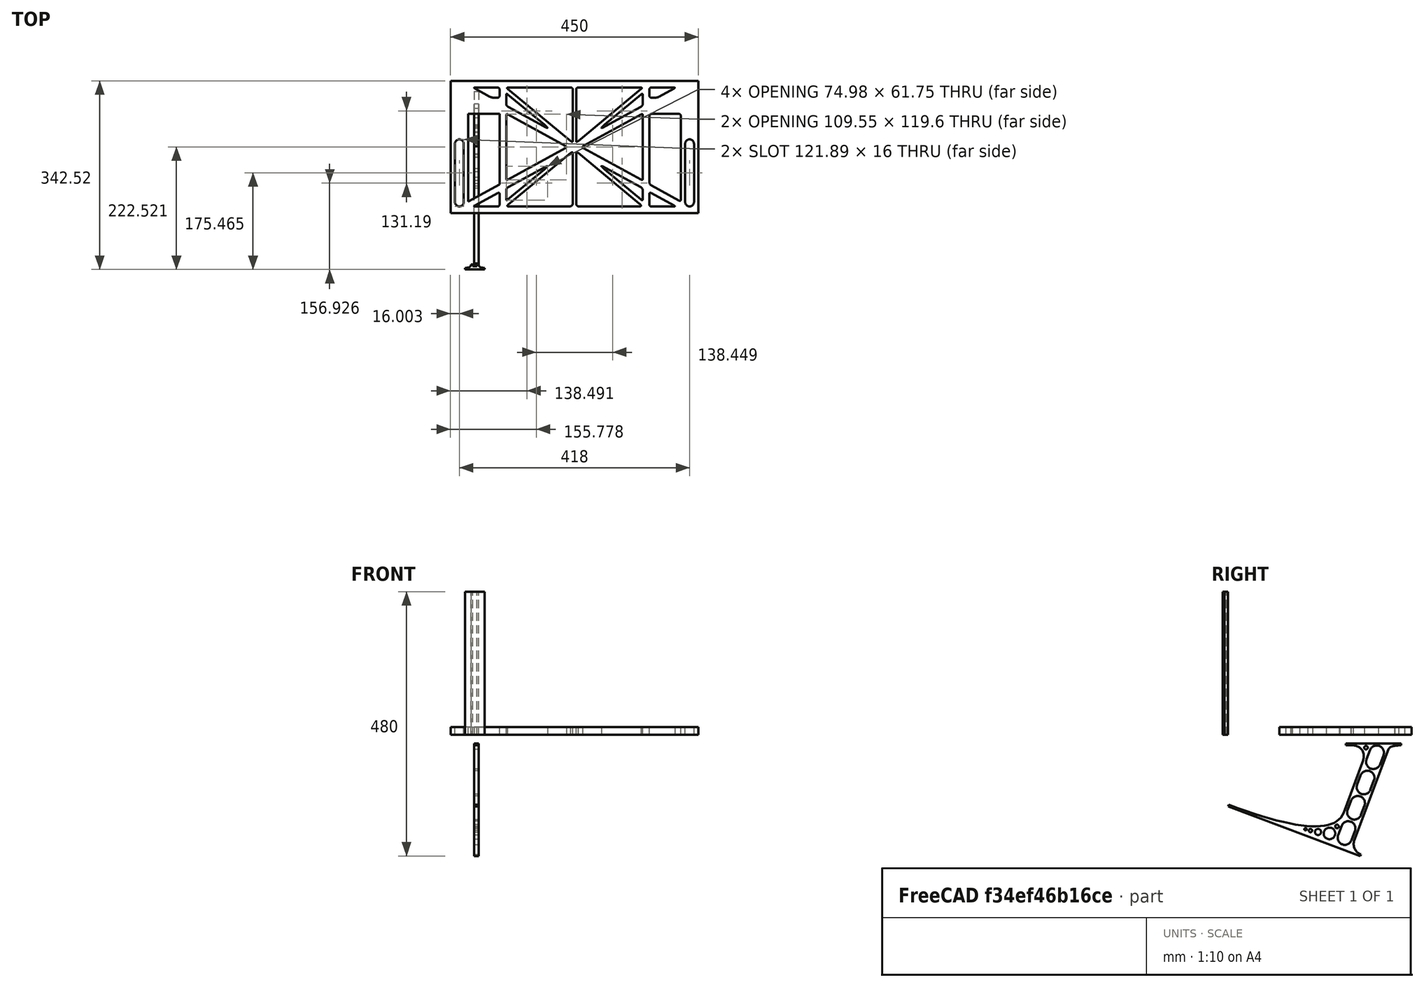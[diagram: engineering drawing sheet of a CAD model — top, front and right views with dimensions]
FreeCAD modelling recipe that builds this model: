
FCSTD DOCUMENT  (FreeCAD 0.19R0.19.2)
Label: laptopStand144FCStd
License: All rights reserved
LicenseURL: http://en.wikipedia.org/wiki/All_rights_reserved
objects: Sketcher::SketchObject×4, Part::Extrusion×3
note: 7 computed .brp shape members not serialized (recipe doc carries the construction recipe); baked Part::Feature solids carry a one-line shape summary decoded from their .brp

FEATURE [Sketcher::SketchObject] Sketch
  FullyConstrained = false
  sketch-geometry (349):
    g0: LineSegment StartX=-10.9272 StartY=-82.7794 StartZ=0 EndX=46.0728 EndY=-51.4823 EndZ=0
    g1: LineSegment StartX=-10.9272 StartY=76.4095 StartZ=0 EndX=-10.9272 EndY=-82.7794 EndZ=0
    g2: LineSegment StartX=46.0728 StartY=76.4095 StartZ=0 EndX=46.0728 EndY=-51.4823 EndZ=0
    g3: LineSegment StartX=-42.9272 StartY=136.221 StartZ=0 EndX=-42.9272 EndY=-103.779 EndZ=0
    g4: LineSegment StartX=407.073 StartY=136.221 StartZ=0 EndX=407.073 EndY=-103.779 EndZ=0
    g5: ArcOfCircle CenterX=-26.9272 CenterY=-83.7794 CenterZ=0 NormalX=0 NormalY=0 NormalZ=1 AngleXU=0 Radius=8 StartAngle=3.14159 EndAngle=6.28319
    g6: ArcOfCircle CenterX=391.073 CenterY=22.1087 CenterZ=0 NormalX=0 NormalY=0 NormalZ=1 AngleXU=0 Radius=8 StartAngle=-4.4e-15 EndAngle=3.14159
    g7: LineSegment StartX=399.073 StartY=22.1087 StartZ=0 EndX=399.073 EndY=-83.7794 EndZ=0
    g8: LineSegment StartX=383.073 StartY=22.1087 StartZ=0 EndX=383.073 EndY=-83.7794 EndZ=0
    g9: ArcOfCircle CenterX=391.073 CenterY=-83.7794 CenterZ=0 NormalX=0 NormalY=0 NormalZ=1 AngleXU=0 Radius=8 StartAngle=3.14159 EndAngle=6.28319
    g10: Circle CenterX=175.022 CenterY=27.0628 CenterZ=0 NormalX=0 NormalY=0 NormalZ=1 AngleXU=0 Radius=1
    g11: Circle CenterX=179.022 CenterY=24.8665 CenterZ=0 NormalX=0 NormalY=0 NormalZ=1 AngleXU=0 Radius=1
    g12: Circle CenterX=179.022 CenterY=27.0628 CenterZ=0 NormalX=0 NormalY=0 NormalZ=1 AngleXU=0 Radius=1
    g13: BSplineCurve PolesCount=3 KnotsCount=2 Degree=2 IsPeriodic=0
    g14: GeomPoint X=175.022 Y=27.0628 Z=0
    g15: GeomPoint X=179.022 Y=27.0628 Z=0
    g16: Circle CenterX=189.124 CenterY=27.0628 CenterZ=0 NormalX=0 NormalY=0 NormalZ=1 AngleXU=0 Radius=1
    g17: Circle CenterX=185.124 CenterY=24.8665 CenterZ=0 NormalX=0 NormalY=0 NormalZ=1 AngleXU=0 Radius=1
    g18: Circle CenterX=185.124 CenterY=27.0628 CenterZ=0 NormalX=0 NormalY=0 NormalZ=1 AngleXU=0 Radius=1
    g19: BSplineCurve PolesCount=3 KnotsCount=2 Degree=2 IsPeriodic=0
    g20: GeomPoint X=189.124 Y=27.0628 Z=0
    g21: GeomPoint X=185.124 Y=27.0628 Z=0
    g22: Circle CenterX=175.022 CenterY=5.37834 CenterZ=0 NormalX=0 NormalY=0 NormalZ=1 AngleXU=0 Radius=1
    g23: Circle CenterX=179.022 CenterY=7.57463 CenterZ=0 NormalX=0 NormalY=0 NormalZ=1 AngleXU=0 Radius=1
    g24: Circle CenterX=179.022 CenterY=5.34704 CenterZ=0 NormalX=0 NormalY=0 NormalZ=1 AngleXU=0 Radius=1
    g25: BSplineCurve PolesCount=3 KnotsCount=2 Degree=2 IsPeriodic=0
    g26: GeomPoint X=175.022 Y=5.37834 Z=0
    g27: GeomPoint X=179.022 Y=5.34704 Z=0
    g28: Circle CenterX=189.124 CenterY=5.37834 CenterZ=0 NormalX=0 NormalY=0 NormalZ=1 AngleXU=0 Radius=1
    g29: Circle CenterX=185.124 CenterY=7.57463 CenterZ=0 NormalX=0 NormalY=0 NormalZ=1 AngleXU=0 Radius=1
    g30: Circle CenterX=185.124 CenterY=5.34704 CenterZ=0 NormalX=0 NormalY=0 NormalZ=1 AngleXU=0 Radius=1
    g31: BSplineCurve PolesCount=3 KnotsCount=2 Degree=2 IsPeriodic=0
    g32: GeomPoint X=189.124 Y=5.37834 Z=0
    g33: GeomPoint X=185.124 Y=5.34704 Z=0
    g34: Circle CenterX=165.871 CenterY=18.1458 CenterZ=0 NormalX=0 NormalY=0 NormalZ=1 AngleXU=0 Radius=1
    g35: Circle CenterX=169.377 CenterY=16.2206 CenterZ=0 NormalX=0 NormalY=0 NormalZ=1 AngleXU=0 Radius=1
    g36: Circle CenterX=165.871 CenterY=14.2954 CenterZ=0 NormalX=0 NormalY=0 NormalZ=1 AngleXU=0 Radius=1
    g37: BSplineCurve PolesCount=3 KnotsCount=2 Degree=2 IsPeriodic=0
    g38: GeomPoint X=165.871 Y=18.1458 Z=0
    g39: GeomPoint X=165.871 Y=14.2954 Z=0
    g40: Circle CenterX=198.275 CenterY=18.1458 CenterZ=0 NormalX=0 NormalY=0 NormalZ=1 AngleXU=0 Radius=1
    g41: Circle CenterX=194.768 CenterY=16.2206 CenterZ=0 NormalX=0 NormalY=0 NormalZ=1 AngleXU=0 Radius=1
    g42: Circle CenterX=198.275 CenterY=14.2954 CenterZ=0 NormalX=0 NormalY=0 NormalZ=1 AngleXU=0 Radius=1
    g43: BSplineCurve PolesCount=3 KnotsCount=2 Degree=2 IsPeriodic=0
    g44: GeomPoint X=198.275 Y=18.1458 Z=0
    g45: GeomPoint X=198.275 Y=14.2954 Z=0
    g46: LineSegment StartX=407.073 StartY=-103.779 StartZ=0 EndX=-42.9272 EndY=-103.779 EndZ=0
    g47: LineSegment StartX=407.073 StartY=136.221 StartZ=0 EndX=-42.9272 EndY=136.221 EndZ=0
    g48: LineSegment StartX=46.0728 StartY=76.4095 StartZ=0 EndX=-10.9272 EndY=76.4095 EndZ=0
    g49: Circle CenterX=125.607 CenterY=54.1951 CenterZ=0 NormalX=0 NormalY=0 NormalZ=1 AngleXU=0 Radius=1
    g50: Circle CenterX=139.632 CenterY=46.4944 CenterZ=0 NormalX=0 NormalY=0 NormalZ=1 AngleXU=0 Radius=1
    g51: Circle CenterX=127.326 CenterY=56.7187 CenterZ=0 NormalX=0 NormalY=0 NormalZ=1 AngleXU=0 Radius=1
    g52: BSplineCurve PolesCount=3 KnotsCount=2 Degree=2 IsPeriodic=0
    g53: GeomPoint X=125.607 Y=54.1951 Z=0
    g54: GeomPoint X=127.326 Y=56.7187 Z=0
    g55: Circle CenterX=236.821 CenterY=56.7187 CenterZ=0 NormalX=0 NormalY=0 NormalZ=1 AngleXU=0 Radius=1
    g56: Circle CenterX=224.513 CenterY=46.4944 CenterZ=0 NormalX=0 NormalY=0 NormalZ=1 AngleXU=0 Radius=1
    g57: Circle CenterX=238.538 CenterY=54.1951 CenterZ=0 NormalX=0 NormalY=0 NormalZ=1 AngleXU=0 Radius=1
    g58: BSplineCurve PolesCount=3 KnotsCount=2 Degree=2 IsPeriodic=0
    g59: GeomPoint X=236.821 Y=56.7187 Z=0
    g60: GeomPoint X=238.538 Y=54.1951 Z=0
    g61: Circle CenterX=238.538 CenterY=-21.7539 CenterZ=0 NormalX=0 NormalY=0 NormalZ=1 AngleXU=0 Radius=1
    g62: Circle CenterX=224.513 CenterY=-14.0532 CenterZ=0 NormalX=0 NormalY=0 NormalZ=1 AngleXU=0 Radius=1
    g63: Circle CenterX=236.821 CenterY=-24.2775 CenterZ=0 NormalX=0 NormalY=0 NormalZ=1 AngleXU=0 Radius=1
    g64: BSplineCurve PolesCount=3 KnotsCount=2 Degree=2 IsPeriodic=0
    g65: GeomPoint X=238.538 Y=-21.7539 Z=0
    g66: GeomPoint X=236.821 Y=-24.2775 Z=0
    g67: Circle CenterX=125.607 CenterY=-21.7539 CenterZ=0 NormalX=0 NormalY=0 NormalZ=1 AngleXU=0 Radius=1
    g68: Circle CenterX=139.632 CenterY=-14.0532 CenterZ=0 NormalX=0 NormalY=0 NormalZ=1 AngleXU=0 Radius=1
    g69: Circle CenterX=127.325 CenterY=-24.2775 CenterZ=0 NormalX=0 NormalY=0 NormalZ=1 AngleXU=0 Radius=1
    g70: BSplineCurve PolesCount=3 KnotsCount=2 Degree=2 IsPeriodic=0
    g71: GeomPoint X=125.607 Y=-21.7539 Z=0
    g72: GeomPoint X=127.325 Y=-24.2775 Z=0
    g73: Circle CenterX=302.996 CenterY=111.695 CenterZ=0 NormalX=0 NormalY=0 NormalZ=1 AngleXU=0 Radius=1
    g74: Circle CenterX=306.073 CenterY=114.251 CenterZ=0 NormalX=0 NormalY=0 NormalZ=1 AngleXU=0 Radius=1
    g75: Circle CenterX=306.073 CenterY=110.251 CenterZ=0 NormalX=0 NormalY=0 NormalZ=1 AngleXU=0 Radius=1
    g76: BSplineCurve PolesCount=3 KnotsCount=2 Degree=2 IsPeriodic=0
    g77: GeomPoint X=302.996 Y=111.695 Z=0
    g78: GeomPoint X=306.073 Y=110.251 Z=0
    g79: Circle CenterX=306.073 CenterY=95.2763 CenterZ=0 NormalX=0 NormalY=0 NormalZ=1 AngleXU=0 Radius=1
    g80: Circle CenterX=306.073 CenterY=91.2763 CenterZ=0 NormalX=0 NormalY=0 NormalZ=1 AngleXU=0 Radius=1
    g81: Circle CenterX=302.567 CenterY=89.3511 CenterZ=0 NormalX=0 NormalY=0 NormalZ=1 AngleXU=0 Radius=1
    g82: BSplineCurve PolesCount=3 KnotsCount=2 Degree=2 IsPeriodic=0
    g83: GeomPoint X=306.073 Y=95.2763 Z=0
    g84: GeomPoint X=302.567 Y=89.3511 Z=0
    g85: LineSegment StartX=306.073 StartY=110.251 StartZ=0 EndX=306.073 EndY=95.2763 EndZ=0
    g86: LineSegment StartX=302.996 StartY=111.695 StartZ=0 EndX=236.821 EndY=56.7187 EndZ=0
    g87: LineSegment StartX=238.538 StartY=54.1951 StartZ=0 EndX=302.567 EndY=89.3511 EndZ=0
    g88: Circle CenterX=61.1496 CenterY=111.695 CenterZ=0 NormalX=0 NormalY=0 NormalZ=1 AngleXU=0 Radius=1
    g89: Circle CenterX=58.0728 CenterY=114.251 CenterZ=0 NormalX=0 NormalY=0 NormalZ=1 AngleXU=0 Radius=1
    g90: Circle CenterX=58.0728 CenterY=110.251 CenterZ=0 NormalX=0 NormalY=0 NormalZ=1 AngleXU=0 Radius=1
    g91: BSplineCurve PolesCount=3 KnotsCount=2 Degree=2 IsPeriodic=0
    g92: GeomPoint X=61.1496 Y=111.695 Z=0
    g93: GeomPoint X=58.0728 Y=110.251 Z=0
    g94: Circle CenterX=61.5791 CenterY=89.3511 CenterZ=0 NormalX=0 NormalY=0 NormalZ=1 AngleXU=0 Radius=1
    g95: Circle CenterX=58.0728 CenterY=91.2763 CenterZ=0 NormalX=0 NormalY=0 NormalZ=1 AngleXU=0 Radius=1
    g96: Circle CenterX=58.0728 CenterY=95.2763 CenterZ=0 NormalX=0 NormalY=0 NormalZ=1 AngleXU=0 Radius=1
    g97: BSplineCurve PolesCount=3 KnotsCount=2 Degree=2 IsPeriodic=0
    g98: GeomPoint X=61.5791 Y=89.3511 Z=0
    g99: GeomPoint X=58.0728 Y=95.2763 Z=0
    g100: LineSegment StartX=58.0728 StartY=110.251 StartZ=0 EndX=58.0728 EndY=95.2763 EndZ=0
    g101: LineSegment StartX=61.1496 StartY=111.695 StartZ=0 EndX=127.326 EndY=56.7187 EndZ=0
    g102: LineSegment StartX=125.607 StartY=54.1951 StartZ=0 EndX=61.5791 EndY=89.3511 EndZ=0
    g103: Circle CenterX=61.5791 CenterY=-56.9099 CenterZ=0 NormalX=0 NormalY=0 NormalZ=1 AngleXU=0 Radius=1
    g104: Circle CenterX=58.0728 CenterY=-58.8351 CenterZ=0 NormalX=0 NormalY=0 NormalZ=1 AngleXU=0 Radius=1
    g105: Circle CenterX=58.0728 CenterY=-62.8351 CenterZ=0 NormalX=0 NormalY=0 NormalZ=1 AngleXU=0 Radius=1
    g106: BSplineCurve PolesCount=3 KnotsCount=2 Degree=2 IsPeriodic=0
    g107: GeomPoint X=61.5791 Y=-56.9099 Z=0
    g108: GeomPoint X=58.0728 Y=-62.8351 Z=0
    g109: Circle CenterX=58.0728 CenterY=-77.8102 CenterZ=0 NormalX=0 NormalY=0 NormalZ=1 AngleXU=0 Radius=1
    g110: Circle CenterX=58.0728 CenterY=-81.8102 CenterZ=0 NormalX=0 NormalY=0 NormalZ=1 AngleXU=0 Radius=1
    g111: Circle CenterX=61.1496 CenterY=-79.2541 CenterZ=0 NormalX=0 NormalY=0 NormalZ=1 AngleXU=0 Radius=1
    g112: BSplineCurve PolesCount=3 KnotsCount=2 Degree=2 IsPeriodic=0
    g113: GeomPoint X=58.0728 Y=-77.8102 Z=0
    g114: GeomPoint X=61.1496 Y=-79.2541 Z=0
    g115: LineSegment StartX=58.0728 StartY=-62.8351 StartZ=0 EndX=58.0728 EndY=-77.8102 EndZ=0
    g116: LineSegment StartX=61.1496 StartY=-79.2541 StartZ=0 EndX=127.325 EndY=-24.2775 EndZ=0
    g117: LineSegment StartX=125.607 StartY=-21.7539 StartZ=0 EndX=61.5791 EndY=-56.9099 EndZ=0
    g118: Circle CenterX=302.567 CenterY=-56.9099 CenterZ=0 NormalX=0 NormalY=0 NormalZ=1 AngleXU=0 Radius=1
    g119: Circle CenterX=306.073 CenterY=-58.8351 CenterZ=0 NormalX=0 NormalY=0 NormalZ=1 AngleXU=0 Radius=1
    g120: Circle CenterX=306.073 CenterY=-62.8351 CenterZ=0 NormalX=0 NormalY=0 NormalZ=1 AngleXU=0 Radius=1
    g121: BSplineCurve PolesCount=3 KnotsCount=2 Degree=2 IsPeriodic=0
    g122: GeomPoint X=302.567 Y=-56.9099 Z=0
    g123: GeomPoint X=306.073 Y=-62.8351 Z=0
    g124: Circle CenterX=302.996 CenterY=-79.2541 CenterZ=0 NormalX=0 NormalY=0 NormalZ=1 AngleXU=0 Radius=1
    g125: Circle CenterX=306.073 CenterY=-81.8102 CenterZ=0 NormalX=0 NormalY=0 NormalZ=1 AngleXU=0 Radius=1
    g126: Circle CenterX=306.073 CenterY=-77.8102 CenterZ=0 NormalX=0 NormalY=0 NormalZ=1 AngleXU=0 Radius=1
    g127: BSplineCurve PolesCount=3 KnotsCount=2 Degree=2 IsPeriodic=0
    g128: GeomPoint X=302.996 Y=-79.2541 Z=0
    g129: GeomPoint X=306.073 Y=-77.8102 Z=0
    g130: LineSegment StartX=306.073 StartY=-62.8351 StartZ=0 EndX=306.073 EndY=-77.8102 EndZ=0
    g131: LineSegment StartX=302.996 StartY=-79.2541 StartZ=0 EndX=236.821 EndY=-24.2775 EndZ=0
    g132: LineSegment StartX=238.538 StartY=-21.7539 StartZ=0 EndX=302.567 EndY=-56.9099 EndZ=0
    g133: Circle CenterX=61.6457 CenterY=-88.8112 CenterZ=0 NormalX=0 NormalY=0 NormalZ=1 AngleXU=0 Radius=1
    g134: Circle CenterX=58.0728 CenterY=-91.7794 CenterZ=0 NormalX=0 NormalY=0 NormalZ=1 AngleXU=0 Radius=1
    g135: Circle CenterX=63.9135 CenterY=-91.7794 CenterZ=0 NormalX=0 NormalY=0 NormalZ=1 AngleXU=0 Radius=1
    g136: BSplineCurve PolesCount=3 KnotsCount=2 Degree=2 IsPeriodic=0
    g137: GeomPoint X=61.6457 Y=-88.8112 Z=0
    g138: GeomPoint X=63.9135 Y=-91.7794 Z=0
    g139: Circle CenterX=179.022 CenterY=-85.8163 CenterZ=0 NormalX=0 NormalY=0 NormalZ=1 AngleXU=0 Radius=1
    g140: Circle CenterX=179.022 CenterY=-91.7794 CenterZ=0 NormalX=0 NormalY=0 NormalZ=1 AngleXU=0 Radius=1
    g141: Circle CenterX=171.895 CenterY=-91.7794 CenterZ=0 NormalX=0 NormalY=0 NormalZ=1 AngleXU=0 Radius=1
    g142: BSplineCurve PolesCount=3 KnotsCount=2 Degree=2 IsPeriodic=0
    g143: GeomPoint X=179.022 Y=-85.8163 Z=0
    g144: GeomPoint X=171.895 Y=-91.7794 Z=0
    g145: Circle CenterX=185.124 CenterY=-86.2028 CenterZ=0 NormalX=0 NormalY=0 NormalZ=1 AngleXU=0 Radius=1
    g146: Circle CenterX=185.124 CenterY=-91.7794 CenterZ=0 NormalX=0 NormalY=0 NormalZ=1 AngleXU=0 Radius=1
    g147: Circle CenterX=191.747 CenterY=-91.7794 CenterZ=0 NormalX=0 NormalY=0 NormalZ=1 AngleXU=0 Radius=1
    g148: BSplineCurve PolesCount=3 KnotsCount=2 Degree=2 IsPeriodic=0
    g149: GeomPoint X=185.124 Y=-86.2028 Z=0
    g150: GeomPoint X=191.747 Y=-91.7794 Z=0
    g151: Circle CenterX=299.888 CenterY=-86.6413 CenterZ=0 NormalX=0 NormalY=0 NormalZ=1 AngleXU=0 Radius=1
    g152: Circle CenterX=306.073 CenterY=-91.7794 CenterZ=0 NormalX=0 NormalY=0 NormalZ=1 AngleXU=0 Radius=1
    g153: Circle CenterX=298.776 CenterY=-91.7794 CenterZ=0 NormalX=0 NormalY=0 NormalZ=1 AngleXU=0 Radius=1
    g154: BSplineCurve PolesCount=3 KnotsCount=2 Degree=2 IsPeriodic=0
    g155: GeomPoint X=299.888 Y=-86.6413 Z=0
    g156: GeomPoint X=298.776 Y=-91.7794 Z=0
    g157: LineSegment StartX=189.124 StartY=5.37834 StartZ=0 EndX=299.888 EndY=-86.6413 EndZ=0
    g158: LineSegment StartX=298.776 StartY=-91.7794 StartZ=0 EndX=191.747 EndY=-91.7794 EndZ=0
    g159: LineSegment StartX=185.124 StartY=-86.2028 StartZ=0 EndX=185.124 EndY=5.34704 EndZ=0
    g160: LineSegment StartX=179.022 StartY=5.34704 StartZ=0 EndX=179.022 EndY=-85.8163 EndZ=0
    g161: LineSegment StartX=171.895 StartY=-91.7794 StartZ=0 EndX=63.9135 EndY=-91.7794 EndZ=0
    g162: LineSegment StartX=61.6457 StartY=-88.8112 StartZ=0 EndX=175.022 EndY=5.37834 EndZ=0
    g163: Circle CenterX=302.073 CenterY=124.221 CenterZ=0 NormalX=0 NormalY=0 NormalZ=1 AngleXU=0 Radius=1
    g164: Circle CenterX=306.073 CenterY=124.221 CenterZ=0 NormalX=0 NormalY=0 NormalZ=1 AngleXU=0 Radius=1
    g165: Circle CenterX=302.996 CenterY=121.665 CenterZ=0 NormalX=0 NormalY=0 NormalZ=1 AngleXU=0 Radius=1
    g166: BSplineCurve PolesCount=3 KnotsCount=2 Degree=2 IsPeriodic=0
    g167: GeomPoint X=302.073 Y=124.221 Z=0
    g168: GeomPoint X=302.996 Y=121.665 Z=0
    g169: Circle CenterX=189.124 CenterY=124.221 CenterZ=0 NormalX=0 NormalY=0 NormalZ=1 AngleXU=0 Radius=1
    g170: Circle CenterX=185.124 CenterY=124.221 CenterZ=0 NormalX=0 NormalY=0 NormalZ=1 AngleXU=0 Radius=1
    g171: Circle CenterX=185.124 CenterY=120.221 CenterZ=0 NormalX=0 NormalY=0 NormalZ=1 AngleXU=0 Radius=1
    g172: BSplineCurve PolesCount=3 KnotsCount=2 Degree=2 IsPeriodic=0
    g173: GeomPoint X=189.124 Y=124.221 Z=0
    g174: GeomPoint X=185.124 Y=120.221 Z=0
    g175: Circle CenterX=175.022 CenterY=124.221 CenterZ=0 NormalX=0 NormalY=0 NormalZ=1 AngleXU=0 Radius=1
    g176: Circle CenterX=179.022 CenterY=124.221 CenterZ=0 NormalX=0 NormalY=0 NormalZ=1 AngleXU=0 Radius=1
    g177: Circle CenterX=179.022 CenterY=120.221 CenterZ=0 NormalX=0 NormalY=0 NormalZ=1 AngleXU=0 Radius=1
    g178: BSplineCurve PolesCount=3 KnotsCount=2 Degree=2 IsPeriodic=0
    g179: GeomPoint X=175.022 Y=124.221 Z=0
    g180: GeomPoint X=179.022 Y=120.221 Z=0
    g181: Circle CenterX=62.0728 CenterY=124.221 CenterZ=0 NormalX=0 NormalY=0 NormalZ=1 AngleXU=0 Radius=1
    g182: Circle CenterX=58.0728 CenterY=124.221 CenterZ=0 NormalX=0 NormalY=0 NormalZ=1 AngleXU=0 Radius=1
    g183: Circle CenterX=61.1496 CenterY=121.665 CenterZ=0 NormalX=0 NormalY=0 NormalZ=1 AngleXU=0 Radius=1
    g184: BSplineCurve PolesCount=3 KnotsCount=2 Degree=2 IsPeriodic=0
    g185: GeomPoint X=62.0728 Y=124.221 Z=0
    g186: GeomPoint X=61.1496 Y=121.665 Z=0
    g187: LineSegment StartX=62.0728 StartY=124.221 StartZ=0 EndX=175.022 EndY=124.221 EndZ=0
    g188: LineSegment StartX=179.022 StartY=120.221 StartZ=0 EndX=179.022 EndY=27.0628 EndZ=0
    g189: LineSegment StartX=185.124 StartY=27.0628 StartZ=0 EndX=185.124 EndY=120.221 EndZ=0
    g190: LineSegment StartX=189.124 StartY=124.221 StartZ=0 EndX=302.073 EndY=124.221 EndZ=0
    g191: LineSegment StartX=302.996 StartY=121.665 StartZ=0 EndX=189.124 EndY=27.0628 EndZ=0
    g192: LineSegment StartX=175.022 StartY=27.0628 StartZ=0 EndX=61.1496 EndY=121.665 EndZ=0
    g193: Circle CenterX=61.5791 CenterY=75.4095 CenterZ=0 NormalX=0 NormalY=0 NormalZ=1 AngleXU=0 Radius=1
    g194: Circle CenterX=58.0728 CenterY=77.3346 CenterZ=0 NormalX=0 NormalY=0 NormalZ=1 AngleXU=0 Radius=1
    g195: Circle CenterX=58.0728 CenterY=73.3346 CenterZ=0 NormalX=0 NormalY=0 NormalZ=1 AngleXU=0 Radius=1
    g196: BSplineCurve PolesCount=3 KnotsCount=2 Degree=2 IsPeriodic=0
    g197: GeomPoint X=61.5791 Y=75.4095 Z=0
    g198: GeomPoint X=58.0728 Y=73.3346 Z=0
    g199: Circle CenterX=58.0728 CenterY=-40.8935 CenterZ=0 NormalX=0 NormalY=0 NormalZ=1 AngleXU=0 Radius=1
    g200: Circle CenterX=58.0728 CenterY=-44.8935 CenterZ=0 NormalX=0 NormalY=0 NormalZ=1 AngleXU=0 Radius=1
    g201: Circle CenterX=61.5791 CenterY=-42.9683 CenterZ=0 NormalX=0 NormalY=0 NormalZ=1 AngleXU=0 Radius=1
    g202: BSplineCurve PolesCount=3 KnotsCount=2 Degree=2 IsPeriodic=0
    g203: GeomPoint X=58.0728 Y=-40.8935 Z=0
    g204: GeomPoint X=61.5791 Y=-42.9683 Z=0
    g205: LineSegment StartX=61.5791 StartY=-42.9683 StartZ=0 EndX=165.871 EndY=14.2954 EndZ=0
    g206: LineSegment StartX=165.871 StartY=18.1458 StartZ=0 EndX=61.5791 EndY=75.4095 EndZ=0
    g207: LineSegment StartX=58.0728 StartY=73.3346 StartZ=0 EndX=58.0728 EndY=-40.8935 EndZ=0
    g208: Circle CenterX=302.567 CenterY=-42.9683 CenterZ=0 NormalX=0 NormalY=0 NormalZ=1 AngleXU=0 Radius=1
    g209: Circle CenterX=306.073 CenterY=-44.8935 CenterZ=0 NormalX=0 NormalY=0 NormalZ=1 AngleXU=0 Radius=1
    g210: Circle CenterX=306.073 CenterY=-40.8935 CenterZ=0 NormalX=0 NormalY=0 NormalZ=1 AngleXU=0 Radius=1
    g211: BSplineCurve PolesCount=3 KnotsCount=2 Degree=2 IsPeriodic=0
    g212: GeomPoint X=302.567 Y=-42.9683 Z=0
    g213: GeomPoint X=306.073 Y=-40.8935 Z=0
    g214: Circle CenterX=306.073 CenterY=73.3346 CenterZ=0 NormalX=0 NormalY=0 NormalZ=1 AngleXU=0 Radius=1
    g215: Circle CenterX=306.073 CenterY=77.3346 CenterZ=0 NormalX=0 NormalY=0 NormalZ=1 AngleXU=0 Radius=1
    g216: Circle CenterX=302.567 CenterY=75.4095 CenterZ=0 NormalX=0 NormalY=0 NormalZ=1 AngleXU=0 Radius=1
    g217: BSplineCurve PolesCount=3 KnotsCount=2 Degree=2 IsPeriodic=0
    g218: GeomPoint X=306.073 Y=73.3346 Z=0
    g219: GeomPoint X=302.567 Y=75.4095 Z=0
    g220: LineSegment StartX=302.567 StartY=-42.9683 StartZ=0 EndX=198.275 EndY=14.2954 EndZ=0
    g221: LineSegment StartX=198.275 StartY=18.1458 StartZ=0 EndX=302.567 EndY=75.4095 EndZ=0
    g222: LineSegment StartX=306.073 StartY=73.3346 StartZ=0 EndX=306.073 EndY=-40.8935 EndZ=0
    g223: LineSegment StartX=322.073 StartY=105.865 StartZ=0 EndX=328.643 EndY=105.865 EndZ=0
    g224: LineSegment StartX=318.073 StartY=120.221 StartZ=0 EndX=318.073 EndY=109.865 EndZ=0
    g225: LineSegment StartX=336.157 StartY=107.779 StartZ=0 EndX=362.567 EndY=122.294 EndZ=0
    g226: Circle CenterX=362.073 CenterY=124.221 CenterZ=0 NormalX=0 NormalY=0 NormalZ=1 AngleXU=0 Radius=1
    g227: Circle CenterX=366.073 CenterY=124.221 CenterZ=0 NormalX=0 NormalY=0 NormalZ=1 AngleXU=0 Radius=1
    g228: Circle CenterX=362.567 CenterY=122.294 CenterZ=0 NormalX=0 NormalY=0 NormalZ=1 AngleXU=0 Radius=1
    g229: BSplineCurve PolesCount=3 KnotsCount=2 Degree=2 IsPeriodic=0
    g230: GeomPoint X=362.073 Y=124.221 Z=0
    g231: GeomPoint X=362.567 Y=122.294 Z=0
    g232: Circle CenterX=322.073 CenterY=124.221 CenterZ=0 NormalX=0 NormalY=0 NormalZ=1 AngleXU=0 Radius=1
    g233: Circle CenterX=318.073 CenterY=124.221 CenterZ=0 NormalX=0 NormalY=0 NormalZ=1 AngleXU=0 Radius=1
    g234: Circle CenterX=318.073 CenterY=120.221 CenterZ=0 NormalX=0 NormalY=0 NormalZ=1 AngleXU=0 Radius=1
    g235: BSplineCurve PolesCount=3 KnotsCount=2 Degree=2 IsPeriodic=0
    g236: GeomPoint X=322.073 Y=124.221 Z=0
    g237: GeomPoint X=318.073 Y=120.221 Z=0
    g238: Circle CenterX=322.073 CenterY=105.865 CenterZ=0 NormalX=0 NormalY=0 NormalZ=1 AngleXU=0 Radius=1
    g239: Circle CenterX=318.073 CenterY=105.865 CenterZ=0 NormalX=0 NormalY=0 NormalZ=1 AngleXU=0 Radius=1
    g240: Circle CenterX=318.073 CenterY=109.865 CenterZ=0 NormalX=0 NormalY=0 NormalZ=1 AngleXU=0 Radius=1
    g241: BSplineCurve PolesCount=3 KnotsCount=2 Degree=2 IsPeriodic=0
    g242: GeomPoint X=322.073 Y=105.865 Z=0
    g243: GeomPoint X=318.073 Y=109.865 Z=0
    g244: Circle CenterX=336.157 CenterY=107.779 CenterZ=0 NormalX=0 NormalY=0 NormalZ=1 AngleXU=0 Radius=1
    g245: Circle CenterX=332.651 CenterY=105.853 CenterZ=0 NormalX=0 NormalY=0 NormalZ=1 AngleXU=0 Radius=1
    g246: Circle CenterX=328.643 CenterY=105.865 CenterZ=0 NormalX=0 NormalY=0 NormalZ=1 AngleXU=0 Radius=1
    g247: BSplineCurve PolesCount=3 KnotsCount=2 Degree=2 IsPeriodic=0
    g248: GeomPoint X=336.157 Y=107.779 Z=0
    g249: GeomPoint X=328.643 Y=105.865 Z=0
    g250: LineSegment StartX=322.073 StartY=124.221 StartZ=0 EndX=362.073 EndY=124.221 EndZ=0
    g251: Circle CenterX=371.567 CenterY=-80.8644 CenterZ=0 NormalX=0 NormalY=0 NormalZ=1 AngleXU=0 Radius=1
    g252: Circle CenterX=375.073 CenterY=-82.7896 CenterZ=0 NormalX=0 NormalY=0 NormalZ=1 AngleXU=0 Radius=1
    g253: Circle CenterX=375.073 CenterY=-78.7896 CenterZ=0 NormalX=0 NormalY=0 NormalZ=1 AngleXU=0 Radius=1
    g254: BSplineCurve PolesCount=3 KnotsCount=2 Degree=2 IsPeriodic=0
    g255: GeomPoint X=371.567 Y=-80.8644 Z=0
    g256: GeomPoint X=375.073 Y=-78.7896 Z=0
    g257: Circle CenterX=321.579 CenterY=-53.4075 CenterZ=0 NormalX=0 NormalY=0 NormalZ=1 AngleXU=0 Radius=1
    g258: Circle CenterX=318.073 CenterY=-51.4823 CenterZ=0 NormalX=0 NormalY=0 NormalZ=1 AngleXU=0 Radius=1
    g259: Circle CenterX=318.073 CenterY=-47.4805 CenterZ=0 NormalX=0 NormalY=0 NormalZ=1 AngleXU=0 Radius=1
    g260: BSplineCurve PolesCount=3 KnotsCount=2 Degree=2 IsPeriodic=0
    g261: GeomPoint X=321.579 Y=-53.4075 Z=0
    g262: GeomPoint X=318.073 Y=-47.4805 Z=0
    g263: LineSegment StartX=371.567 StartY=-80.8644 StartZ=0 EndX=321.579 EndY=-53.4075 EndZ=0
    g264: Circle CenterX=321.579 CenterY=-67.3492 CenterZ=0 NormalX=0 NormalY=0 NormalZ=1 AngleXU=0 Radius=1
    g265: Circle CenterX=318.073 CenterY=-65.424 CenterZ=0 NormalX=0 NormalY=0 NormalZ=1 AngleXU=0 Radius=1
    g266: Circle CenterX=318.073 CenterY=-69.424 CenterZ=0 NormalX=0 NormalY=0 NormalZ=1 AngleXU=0 Radius=1
    g267: BSplineCurve PolesCount=3 KnotsCount=2 Degree=2 IsPeriodic=0
    g268: GeomPoint X=321.579 Y=-67.3492 Z=0
    g269: GeomPoint X=318.073 Y=-69.424 Z=0
    g270: Circle CenterX=362.567 CenterY=-89.8542 CenterZ=0 NormalX=0 NormalY=0 NormalZ=1 AngleXU=0 Radius=1
    g271: Circle CenterX=366.073 CenterY=-91.7794 CenterZ=0 NormalX=0 NormalY=0 NormalZ=1 AngleXU=0 Radius=1
    g272: Circle CenterX=362.073 CenterY=-91.7794 CenterZ=0 NormalX=0 NormalY=0 NormalZ=1 AngleXU=0 Radius=1
    g273: BSplineCurve PolesCount=3 KnotsCount=2 Degree=2 IsPeriodic=0
    g274: GeomPoint X=362.567 Y=-89.8542 Z=0
    g275: GeomPoint X=362.073 Y=-91.7794 Z=0
    g276: Circle CenterX=322.073 CenterY=-91.7794 CenterZ=0 NormalX=0 NormalY=0 NormalZ=1 AngleXU=0 Radius=1
    g277: Circle CenterX=318.073 CenterY=-91.7794 CenterZ=0 NormalX=0 NormalY=0 NormalZ=1 AngleXU=0 Radius=1
    g278: Circle CenterX=318.073 CenterY=-87.7794 CenterZ=0 NormalX=0 NormalY=0 NormalZ=1 AngleXU=0 Radius=1
    g279: BSplineCurve PolesCount=3 KnotsCount=2 Degree=2 IsPeriodic=0
    g280: GeomPoint X=322.073 Y=-91.7794 Z=0
    g281: GeomPoint X=318.073 Y=-87.7794 Z=0
    g282: LineSegment StartX=362.567 StartY=-89.8542 StartZ=0 EndX=321.579 EndY=-67.3492 EndZ=0
    g283: LineSegment StartX=318.073 StartY=-69.424 StartZ=0 EndX=318.073 EndY=-87.7794 EndZ=0
    g284: LineSegment StartX=322.073 StartY=-91.7794 StartZ=0 EndX=362.073 EndY=-91.7794 EndZ=0
    g285: Circle CenterX=2.07281 CenterY=124.221 CenterZ=0 NormalX=0 NormalY=0 NormalZ=1 AngleXU=0 Radius=1
    g286: Circle CenterX=1.57905 CenterY=122.295 CenterZ=0 NormalX=0 NormalY=0 NormalZ=1 AngleXU=0 Radius=1
    g287: BSplineCurve PolesCount=3 KnotsCount=2 Degree=2 IsPeriodic=0
    g288: GeomPoint X=2.07281 Y=124.221 Z=0
    g289: GeomPoint X=1.57905 Y=122.295 Z=0
    g290: Circle CenterX=42.0728 CenterY=124.221 CenterZ=0 NormalX=0 NormalY=0 NormalZ=1 AngleXU=0 Radius=1
    g291: Circle CenterX=46.0728 CenterY=124.221 CenterZ=0 NormalX=0 NormalY=0 NormalZ=1 AngleXU=0 Radius=1
    g292: Circle CenterX=46.0728 CenterY=120.221 CenterZ=0 NormalX=0 NormalY=0 NormalZ=1 AngleXU=0 Radius=1
    g293: BSplineCurve PolesCount=3 KnotsCount=2 Degree=2 IsPeriodic=0
    g294: GeomPoint X=42.0728 Y=124.221 Z=0
    g295: GeomPoint X=46.0728 Y=120.221 Z=0
    g296: Circle CenterX=46.0728 CenterY=109.865 CenterZ=0 NormalX=0 NormalY=0 NormalZ=1 AngleXU=0 Radius=1
    g297: Circle CenterX=46.0728 CenterY=105.865 CenterZ=0 NormalX=0 NormalY=0 NormalZ=1 AngleXU=0 Radius=1
    g298: Circle CenterX=42.0728 CenterY=105.865 CenterZ=0 NormalX=0 NormalY=0 NormalZ=1 AngleXU=0 Radius=1
    g299: BSplineCurve PolesCount=3 KnotsCount=2 Degree=2 IsPeriodic=0
    g300: GeomPoint X=46.0728 Y=109.865 Z=0
    g301: GeomPoint X=42.0728 Y=105.865 Z=0
    g302: Circle CenterX=35.5028 CenterY=105.865 CenterZ=0 NormalX=0 NormalY=0 NormalZ=1 AngleXU=0 Radius=1
    g303: Circle CenterX=31.5028 CenterY=105.865 CenterZ=0 NormalX=0 NormalY=0 NormalZ=1 AngleXU=0 Radius=1
    g304: Circle CenterX=27.9965 CenterY=107.79 CenterZ=0 NormalX=0 NormalY=0 NormalZ=1 AngleXU=0 Radius=1
    g305: BSplineCurve PolesCount=3 KnotsCount=2 Degree=2 IsPeriodic=0
    g306: GeomPoint X=35.5028 Y=105.865 Z=0
    g307: GeomPoint X=27.9965 Y=107.79 Z=0
    g308: LineSegment StartX=2.07281 StartY=124.221 StartZ=0 EndX=42.0728 EndY=124.221 EndZ=0
    g309: LineSegment StartX=46.0728 StartY=120.221 StartZ=0 EndX=46.0728 EndY=109.865 EndZ=0
    g310: LineSegment StartX=42.0728 StartY=105.865 StartZ=0 EndX=35.5028 EndY=105.865 EndZ=0
    g311: LineSegment StartX=27.9965 StartY=107.79 StartZ=0 EndX=1.57905 EndY=122.295 EndZ=0
    g312: Circle CenterX=42.5666 CenterY=-67.3492 CenterZ=0 NormalX=0 NormalY=0 NormalZ=1 AngleXU=0 Radius=1
    g313: Circle CenterX=46.0728 CenterY=-65.424 CenterZ=0 NormalX=0 NormalY=0 NormalZ=1 AngleXU=0 Radius=1
    g314: Circle CenterX=46.0728 CenterY=-69.424 CenterZ=0 NormalX=0 NormalY=0 NormalZ=1 AngleXU=0 Radius=1
    g315: BSplineCurve PolesCount=3 KnotsCount=2 Degree=2 IsPeriodic=0
    g316: GeomPoint X=42.5666 Y=-67.3492 Z=0
    g317: GeomPoint X=46.0728 Y=-69.424 Z=0
    g318: Circle CenterX=46.0728 CenterY=-87.7794 CenterZ=0 NormalX=0 NormalY=0 NormalZ=1 AngleXU=0 Radius=1
    g319: Circle CenterX=46.0728 CenterY=-91.7794 CenterZ=0 NormalX=0 NormalY=0 NormalZ=1 AngleXU=0 Radius=1
    g320: Circle CenterX=42.0728 CenterY=-91.7794 CenterZ=0 NormalX=0 NormalY=0 NormalZ=1 AngleXU=0 Radius=1
    g321: BSplineCurve PolesCount=3 KnotsCount=2 Degree=2 IsPeriodic=0
    g322: GeomPoint X=46.0728 Y=-87.7794 Z=0
    g323: GeomPoint X=42.0728 Y=-91.7794 Z=0
    g324: Circle CenterX=2.07281 CenterY=-91.7794 CenterZ=0 NormalX=0 NormalY=0 NormalZ=1 AngleXU=0 Radius=1
    g325: Circle CenterX=-1.92719 CenterY=-91.7794 CenterZ=0 NormalX=0 NormalY=0 NormalZ=1 AngleXU=0 Radius=1
    g326: Circle CenterX=1.57905 CenterY=-89.8542 CenterZ=0 NormalX=0 NormalY=0 NormalZ=1 AngleXU=0 Radius=1
    g327: BSplineCurve PolesCount=3 KnotsCount=2 Degree=2 IsPeriodic=0
    g328: GeomPoint X=2.07281 Y=-91.7794 Z=0
    g329: GeomPoint X=1.57905 Y=-89.8542 Z=0
    g330: LineSegment StartX=2.07281 StartY=-91.7794 StartZ=0 EndX=42.0728 EndY=-91.7794 EndZ=0
    g331: LineSegment StartX=46.0728 StartY=-87.7794 StartZ=0 EndX=46.0728 EndY=-69.424 EndZ=0
    g332: LineSegment StartX=42.5666 StartY=-67.3492 StartZ=0 EndX=1.57905 EndY=-89.8542 EndZ=0
    g333: Circle CenterX=322.073 CenterY=76.4095 CenterZ=0 NormalX=0 NormalY=0 NormalZ=1 AngleXU=0 Radius=4
    g334: BSplineCurve PolesCount=3 KnotsCount=2 Degree=2 IsPeriodic=0
    g335: GeomPoint X=318.073 Y=72.4095 Z=0
    g336: GeomPoint X=322.073 Y=76.4095 Z=0
    g337: Circle CenterX=375.073 CenterY=72.4095 CenterZ=0 NormalX=0 NormalY=0 NormalZ=1 AngleXU=0 Radius=1
    g338: Circle CenterX=375.073 CenterY=76.4095 CenterZ=0 NormalX=0 NormalY=0 NormalZ=1 AngleXU=0 Radius=1
    g339: Circle CenterX=371.073 CenterY=76.4095 CenterZ=0 NormalX=0 NormalY=0 NormalZ=1 AngleXU=0 Radius=1
    g340: BSplineCurve PolesCount=3 KnotsCount=2 Degree=2 IsPeriodic=0
    g341: GeomPoint X=375.073 Y=72.4095 Z=0
    g342: GeomPoint X=371.073 Y=76.4095 Z=0
    g343: LineSegment StartX=322.073 StartY=76.4095 StartZ=0 EndX=371.073 EndY=76.4095 EndZ=0
    g344: LineSegment StartX=318.073 StartY=72.4095 StartZ=0 EndX=318.073 EndY=-47.4805 EndZ=0
    g345: LineSegment StartX=375.073 StartY=72.4095 StartZ=0 EndX=375.073 EndY=-78.7896 EndZ=0
    g346: ArcOfCircle CenterX=-26.9272 CenterY=22.1087 CenterZ=0 NormalX=0 NormalY=0 NormalZ=1 AngleXU=0 Radius=4 StartAngle=5e-16 EndAngle=3.14159
    g347: LineSegment StartX=-30.9272 StartY=22.1087 StartZ=0 EndX=-34.9272 EndY=-83.7794 EndZ=0
    g348: LineSegment StartX=-18.9272 StartY=-83.7794 StartZ=0 EndX=-22.9272 EndY=22.1087 EndZ=0
  constraints (572):
    c: Coincident(g0,g2)
    c: Block(g0)
    c: Block(g1)
    c: Vertical(g3)
    c: Vertical(g4)
    c: Block(g4)
    c: Block(g3)
    c: Tangent(g6,g7) = 1.5708
    c: Tangent(g7,g9) = 1.5708
    c: Equal(g6,g9)
    c: Coincident(g8,g6)
    c: Coincident(g8,g9)
    c: Block(g7)
    c: Block(g8)
    c: Weight(g10) = 1
    c: Equal(g10,g11)
    c: Equal(g10,g12)
    c: InternalAlignment(g10,g13)
    c: InternalAlignment(g11,g13)
    c: InternalAlignment(g12,g13)
    c: InternalAlignment(g14,g13)
    c: InternalAlignment(g15,g13)
    c: Weight(g16) = 1
    c: Equal(g16,g17)
    c: Equal(g16,g18)
    c: InternalAlignment(g16,g19)
    c: InternalAlignment(g17,g19)
    c: InternalAlignment(g18,g19)
    c: InternalAlignment(g20,g19)
    c: InternalAlignment(g21,g19)
    c: Block(g19)
    c: Block(g13)
    c: Weight(g22) = 1
    c: Equal(g22,g23)
    c: Equal(g22,g24)
    c: InternalAlignment(g22,g25)
    c: InternalAlignment(g23,g25)
    c: InternalAlignment(g24,g25)
    c: InternalAlignment(g26,g25)
    c: InternalAlignment(g27,g25)
    c: Weight(g28) = 1
    c: Equal(g28,g29)
    c: Equal(g28,g30)
    c: InternalAlignment(g28,g31)
    c: InternalAlignment(g29,g31)
    c: InternalAlignment(g30,g31)
    c: InternalAlignment(g32,g31)
    c: InternalAlignment(g33,g31)
    c: Block(g31)
    c: Block(g25)
    c: Weight(g34) = 1
    c: Equal(g34,g35)
    c: Equal(g34,g36)
    c: InternalAlignment(g34,g37)
    c: InternalAlignment(g35,g37)
    c: InternalAlignment(g36,g37)
    c: InternalAlignment(g38,g37)
    c: InternalAlignment(g39,g37)
    c: Weight(g40) = 1
    c: Equal(g40,g41)
    c: Equal(g40,g42)
    c: InternalAlignment(g40,g43)
    c: InternalAlignment(g41,g43)
    c: InternalAlignment(g42,g43)
    c: InternalAlignment(g44,g43)
    c: InternalAlignment(g45,g43)
    c: Block(g37)
    c: Block(g43)
    c: Coincident(g46,g4)
    c: Coincident(g46,g3)
    c: Horizontal(g46)
    c: Distance(g46) = 450
    c: Coincident(g47,g4)
    c: Coincident(g47,g3)
    c: Horizontal(g47)
    c: Horizontal(g48)
    c: Coincident(g2,g48)
    c: Block(g48)
    c: Coincident(g1,g48)
    c: Weight(g49) = 1
    c: Equal(g49,g50)
    c: Equal(g49,g51)
    c: InternalAlignment(g49,g52)
    c: InternalAlignment(g50,g52)
    c: InternalAlignment(g51,g52)
    c: InternalAlignment(g53,g52)
    c: InternalAlignment(g54,g52)
    c: Block(g52)
    c: Weight(g55) = 1
    c: Equal(g55,g56)
    c: Equal(g55,g57)
    c: InternalAlignment(g55,g58)
    c: InternalAlignment(g56,g58)
    c: InternalAlignment(g57,g58)
    c: InternalAlignment(g59,g58)
    c: InternalAlignment(g60,g58)
    c: Block(g58)
    c: Weight(g61) = 1
    c: Equal(g61,g62)
    c: Equal(g61,g63)
    c: InternalAlignment(g61,g64)
    c: InternalAlignment(g62,g64)
    c: InternalAlignment(g63,g64)
    c: InternalAlignment(g65,g64)
    c: InternalAlignment(g66,g64)
    c: Block(g64)
    c: Weight(g67) = 1
    c: Equal(g67,g68)
    c: Equal(g67,g69)
    c: InternalAlignment(g67,g70)
    c: InternalAlignment(g68,g70)
    c: InternalAlignment(g69,g70)
    c: InternalAlignment(g71,g70)
    c: InternalAlignment(g72,g70)
    c: Block(g70)
    c: Weight(g73) = 1
    c: Equal(g73,g74)
    c: Equal(g73,g75)
    c: InternalAlignment(g73,g76)
    c: InternalAlignment(g74,g76)
    c: InternalAlignment(g75,g76)
    c: InternalAlignment(g77,g76)
    c: InternalAlignment(g78,g76)
    c: Weight(g79) = 1
    c: Equal(g79,g80)
    c: Equal(g79,g81)
    c: InternalAlignment(g79,g82)
    c: InternalAlignment(g80,g82)
    c: InternalAlignment(g81,g82)
    c: InternalAlignment(g83,g82)
    c: InternalAlignment(g84,g82)
    c: Block(g76)
    c: Block(g82)
    c: Coincident(g85,g76)
    c: Coincident(g85,g82)
    c: Vertical(g85)
    c: Coincident(g86,g76)
    c: Coincident(g86,g58)
    c: Coincident(g87,g58)
    c: Coincident(g87,g82)
    c: Weight(g88) = 1
    c: Equal(g88,g89)
    c: Equal(g88,g90)
    c: InternalAlignment(g88,g91)
    c: InternalAlignment(g89,g91)
    c: InternalAlignment(g90,g91)
    c: InternalAlignment(g92,g91)
    c: InternalAlignment(g93,g91)
    c: Weight(g94) = 1
    c: Equal(g94,g95)
    c: Equal(g94,g96)
    c: InternalAlignment(g94,g97)
    c: InternalAlignment(g95,g97)
    c: InternalAlignment(g96,g97)
    c: InternalAlignment(g98,g97)
    c: InternalAlignment(g99,g97)
    c: Block(g91)
    c: Block(g97)
    c: Coincident(g100,g91)
    c: Coincident(g100,g97)
    c: Vertical(g100)
    c: Coincident(g101,g91)
    c: Coincident(g101,g52)
    c: Coincident(g102,g52)
    c: Coincident(g102,g97)
    c: Weight(g103) = 1
    c: Equal(g103,g104)
    c: Equal(g103,g105)
    c: InternalAlignment(g103,g106)
    c: InternalAlignment(g104,g106)
    c: InternalAlignment(g105,g106)
    c: InternalAlignment(g107,g106)
    c: InternalAlignment(g108,g106)
    c: Weight(g109) = 1
    c: Equal(g109,g110)
    c: Equal(g109,g111)
    c: InternalAlignment(g109,g112)
    c: InternalAlignment(g110,g112)
    c: InternalAlignment(g111,g112)
    c: InternalAlignment(g113,g112)
    c: InternalAlignment(g114,g112)
    c: Block(g106)
    c: Block(g112)
    c: Coincident(g115,g106)
    c: Coincident(g115,g112)
    c: Vertical(g115)
    c: Coincident(g116,g112)
    c: Coincident(g116,g70)
    c: Coincident(g117,g70)
    c: Coincident(g117,g106)
    c: Weight(g118) = 1
    c: Equal(g118,g119)
    c: Equal(g118,g120)
    c: InternalAlignment(g118,g121)
    c: InternalAlignment(g119,g121)
    c: InternalAlignment(g120,g121)
    c: InternalAlignment(g122,g121)
    c: InternalAlignment(g123,g121)
    c: Weight(g124) = 1
    c: Equal(g124,g125)
    c: Equal(g124,g126)
    c: InternalAlignment(g124,g127)
    c: InternalAlignment(g125,g127)
    c: InternalAlignment(g126,g127)
    c: InternalAlignment(g128,g127)
    c: InternalAlignment(g129,g127)
    c: Block(g121)
    c: Block(g127)
    c: Coincident(g130,g121)
    c: Coincident(g130,g127)
    c: Vertical(g130)
    c: Coincident(g131,g127)
    c: Coincident(g131,g64)
    c: Coincident(g132,g64)
    c: Coincident(g132,g121)
    c: Weight(g133) = 1
    c: Equal(g133,g134)
    c: Equal(g133,g135)
    c: InternalAlignment(g133,g136)
    c: InternalAlignment(g134,g136)
    c: InternalAlignment(g135,g136)
    c: InternalAlignment(g137,g136)
    c: InternalAlignment(g138,g136)
    c: Weight(g139) = 1
    c: Equal(g139,g140)
    c: Equal(g139,g141)
    c: InternalAlignment(g139,g142)
    c: InternalAlignment(g140,g142)
    c: InternalAlignment(g141,g142)
    c: InternalAlignment(g143,g142)
    c: InternalAlignment(g144,g142)
    c: Weight(g145) = 1
    c: Equal(g145,g146)
    c: Equal(g145,g147)
    c: InternalAlignment(g145,g148)
    c: InternalAlignment(g146,g148)
    c: InternalAlignment(g147,g148)
    c: InternalAlignment(g149,g148)
    c: InternalAlignment(g150,g148)
    c: Weight(g151) = 1
    c: Equal(g151,g152)
    c: Equal(g151,g153)
    c: InternalAlignment(g151,g154)
    c: InternalAlignment(g152,g154)
    c: InternalAlignment(g153,g154)
    c: InternalAlignment(g155,g154)
    c: InternalAlignment(g156,g154)
    c: Block(g154)
    c: Block(g148)
    c: Block(g142)
    c: Block(g136)
    c: Coincident(g157,g31)
    c: Coincident(g157,g154)
    c: Coincident(g158,g154)
    c: Coincident(g158,g148)
    c: Horizontal(g158)
    c: Coincident(g159,g148)
    c: Coincident(g159,g31)
    c: Vertical(g159)
    c: Coincident(g160,g25)
    c: Coincident(g160,g142)
    c: Vertical(g160)
    c: Coincident(g161,g142)
    c: Coincident(g161,g136)
    c: Horizontal(g161)
    c: Coincident(g162,g136)
    c: Coincident(g162,g25)
    c: Weight(g163) = 1
    c: Equal(g163,g164)
    c: Equal(g163,g165)
    c: InternalAlignment(g163,g166)
    c: InternalAlignment(g164,g166)
    c: InternalAlignment(g165,g166)
    c: InternalAlignment(g167,g166)
    c: InternalAlignment(g168,g166)
    c: Weight(g169) = 1
    c: Equal(g169,g170)
    c: Equal(g169,g171)
    c: InternalAlignment(g169,g172)
    c: InternalAlignment(g170,g172)
    c: InternalAlignment(g171,g172)
    c: InternalAlignment(g173,g172)
    c: InternalAlignment(g174,g172)
    c: Weight(g175) = 1
    c: Equal(g175,g176)
    c: Equal(g175,g177)
    c: InternalAlignment(g175,g178)
    c: InternalAlignment(g176,g178)
    c: InternalAlignment(g177,g178)
    c: InternalAlignment(g179,g178)
    c: InternalAlignment(g180,g178)
    c: Weight(g181) = 1
    c: Equal(g181,g182)
    c: Equal(g181,g183)
    c: InternalAlignment(g181,g184)
    c: InternalAlignment(g182,g184)
    c: InternalAlignment(g183,g184)
    c: InternalAlignment(g185,g184)
    c: InternalAlignment(g186,g184)
    c: Block(g184)
    c: Block(g178)
    c: Block(g172)
    c: Block(g166)
    c: Coincident(g187,g184)
    c: Coincident(g187,g178)
    c: Horizontal(g187)
    c: Coincident(g188,g178)
    c: Coincident(g188,g13)
    c: Vertical(g188)
    c: Coincident(g189,g19)
    c: Coincident(g189,g172)
    c: Vertical(g189)
    c: Coincident(g190,g172)
    c: Coincident(g190,g166)
    c: Horizontal(g190)
    c: Coincident(g191,g166)
    c: Coincident(g191,g19)
    c: Coincident(g192,g13)
    c: Weight(g193) = 1
    c: Equal(g193,g194)
    c: Equal(g193,g195)
    c: InternalAlignment(g193,g196)
    c: InternalAlignment(g194,g196)
    c: InternalAlignment(g195,g196)
    c: InternalAlignment(g197,g196)
    c: InternalAlignment(g198,g196)
    c: Weight(g199) = 1
    c: Equal(g199,g200)
    c: Equal(g199,g201)
    c: InternalAlignment(g199,g202)
    c: InternalAlignment(g200,g202)
    c: InternalAlignment(g201,g202)
    c: InternalAlignment(g203,g202)
    c: InternalAlignment(g204,g202)
    c: Block(g202)
    c: Block(g196)
    c: Coincident(g205,g202)
    c: Coincident(g205,g37)
    c: Coincident(g206,g37)
    c: Coincident(g206,g196)
    c: Coincident(g207,g196)
    c: Coincident(g207,g202)
    c: Vertical(g207)
    c: Weight(g208) = 1
    c: Equal(g208,g209)
    c: Equal(g208,g210)
    c: InternalAlignment(g208,g211)
    c: InternalAlignment(g209,g211)
    c: InternalAlignment(g210,g211)
    c: InternalAlignment(g212,g211)
    c: InternalAlignment(g213,g211)
    c: Weight(g214) = 1
    c: Equal(g214,g215)
    c: Equal(g214,g216)
    c: InternalAlignment(g214,g217)
    c: InternalAlignment(g215,g217)
    c: InternalAlignment(g216,g217)
    c: InternalAlignment(g218,g217)
    c: InternalAlignment(g219,g217)
    c: Block(g217)
    c: Block(g211)
    c: Coincident(g220,g211)
    c: Coincident(g220,g43)
    c: Coincident(g221,g43)
    c: Coincident(g221,g217)
    c: Coincident(g222,g217)
    c: Coincident(g222,g211)
    c: Vertical(g222)
    c: Horizontal(g223)
    c: Block(g223)
    c: Vertical(g224)
    c: Block(g224)
    c: Block(g225)
    c: Weight(g226) = 1
    c: Equal(g226,g227)
    c: Equal(g226,g228)
    c: InternalAlignment(g226,g229)
    c: InternalAlignment(g227,g229)
    c: InternalAlignment(g228,g229)
    c: InternalAlignment(g230,g229)
    c: InternalAlignment(g231,g229)
    c: Weight(g232) = 1
    c: Equal(g232,g233)
    c: Equal(g232,g234)
    c: InternalAlignment(g232,g235)
    c: InternalAlignment(g233,g235)
    c: InternalAlignment(g234,g235)
    c: InternalAlignment(g236,g235)
    c: InternalAlignment(g237,g235)
    c: Weight(g238) = 1
    c: Equal(g238,g239)
    c: Equal(g238,g240)
    c: InternalAlignment(g238,g241)
    c: InternalAlignment(g239,g241)
    c: InternalAlignment(g240,g241)
    c: InternalAlignment(g242,g241)
    c: InternalAlignment(g243,g241)
    c: Weight(g244) = 1
    c: Equal(g244,g245)
    c: Equal(g244,g246)
    c: InternalAlignment(g244,g247)
    c: InternalAlignment(g245,g247)
    c: InternalAlignment(g246,g247)
    c: InternalAlignment(g248,g247)
    c: InternalAlignment(g249,g247)
    c: Block(g229)
    c: Block(g235)
    c: Block(g241)
    c: Block(g247)
    c: Coincident(g250,g235)
    c: Coincident(g250,g229)
    c: Horizontal(g250)
    c: Block(g192)
    c: Weight(g251) = 1
    c: Equal(g251,g252)
    c: Equal(g251,g253)
    c: InternalAlignment(g251,g254)
    c: InternalAlignment(g252,g254)
    c: InternalAlignment(g253,g254)
    c: InternalAlignment(g255,g254)
    c: InternalAlignment(g256,g254)
    c: Weight(g257) = 1
    c: Equal(g257,g258)
    c: Equal(g257,g259)
    c: InternalAlignment(g257,g260)
    c: InternalAlignment(g258,g260)
    c: InternalAlignment(g259,g260)
    c: InternalAlignment(g261,g260)
    c: InternalAlignment(g262,g260)
    c: Block(g254)
    c: Block(g260)
    c: Coincident(g263,g254)
    c: Coincident(g263,g260)
    c: Weight(g264) = 1
    c: Equal(g264,g265)
    c: Equal(g264,g266)
    c: InternalAlignment(g264,g267)
    c: InternalAlignment(g265,g267)
    c: InternalAlignment(g266,g267)
    c: InternalAlignment(g268,g267)
    c: InternalAlignment(g269,g267)
    c: Weight(g270) = 1
    c: Equal(g270,g271)
    c: Equal(g270,g272)
    c: InternalAlignment(g270,g273)
    c: InternalAlignment(g271,g273)
    c: InternalAlignment(g272,g273)
    c: InternalAlignment(g274,g273)
    c: InternalAlignment(g275,g273)
    c: Weight(g276) = 1
    c: Equal(g276,g277)
    c: Equal(g276,g278)
    c: InternalAlignment(g276,g279)
    c: InternalAlignment(g277,g279)
    c: InternalAlignment(g278,g279)
    c: InternalAlignment(g280,g279)
    c: InternalAlignment(g281,g279)
    c: Block(g279)
    c: Block(g273)
    c: Block(g267)
    c: Coincident(g282,g273)
    c: Coincident(g282,g267)
    c: Coincident(g283,g267)
    c: Coincident(g283,g279)
    c: Vertical(g283)
    c: Coincident(g284,g279)
    c: Coincident(g284,g273)
    c: Horizontal(g284)
    c: Weight(g285) = 1
    c: Equal(g285,g286)
    c: InternalAlignment(g285,g287)
    c: InternalAlignment(g286,g287)
    c: InternalAlignment(g288,g287)
    c: InternalAlignment(g289,g287)
    c: Weight(g290) = 1
    c: InternalAlignment(g291,g293)
    c: InternalAlignment(g292,g293)
    c: InternalAlignment(g294,g293)
    c: InternalAlignment(g295,g293)
    c: Weight(g296) = 1
    c: Equal(g296,g297)
    c: Equal(g296,g298)
    c: InternalAlignment(g296,g299)
    c: InternalAlignment(g297,g299)
    c: InternalAlignment(g298,g299)
    c: InternalAlignment(g300,g299)
    c: InternalAlignment(g301,g299)
    c: Equal(g302,g303)
    c: Equal(g302,g304)
    c: InternalAlignment(g302,g305)
    c: InternalAlignment(g303,g305)
    c: InternalAlignment(g304,g305)
    c: InternalAlignment(g306,g305)
    c: InternalAlignment(g307,g305)
    c: Block(g293)
    c: Block(g299)
    c: Block(g305)
    c: Block(g287)
    c: Coincident(g308,g287)
    c: Coincident(g308,g293)
    c: Horizontal(g308)
    c: Coincident(g309,g293)
    c: Coincident(g309,g299)
    c: Vertical(g309)
    c: Coincident(g310,g299)
    c: Coincident(g310,g305)
    c: Horizontal(g310)
    c: Coincident(g311,g305)
    c: Coincident(g311,g287)
    c: Weight(g312) = 1
    c: Equal(g312,g313)
    c: Equal(g312,g314)
    c: InternalAlignment(g312,g315)
    c: InternalAlignment(g313,g315)
    c: InternalAlignment(g314,g315)
    c: InternalAlignment(g316,g315)
    c: InternalAlignment(g317,g315)
    c: Weight(g318) = 1
    c: Equal(g318,g319)
    c: Equal(g318,g320)
    c: InternalAlignment(g318,g321)
    c: InternalAlignment(g319,g321)
    c: InternalAlignment(g320,g321)
    c: InternalAlignment(g322,g321)
    c: InternalAlignment(g323,g321)
    c: Weight(g324) = 1
    c: Equal(g324,g325)
    c: Equal(g324,g326)
    c: InternalAlignment(g324,g327)
    c: InternalAlignment(g325,g327)
    c: InternalAlignment(g326,g327)
    c: InternalAlignment(g328,g327)
    c: InternalAlignment(g329,g327)
    c: Block(g327)
    c: Block(g321)
    c: Block(g315)
    c: Coincident(g330,g327)
    c: Coincident(g330,g321)
    c: Horizontal(g330)
    c: Coincident(g331,g321)
    c: Coincident(g331,g315)
    c: Vertical(g331)
    c: Coincident(g332,g315)
    c: Coincident(g332,g327)
    c: InternalAlignment(g333,g334)
    c: InternalAlignment(g335,g334)
    c: InternalAlignment(g336,g334)
    c: Block(g334)
    c: Equal(g337,g338)
    c: Equal(g337,g339)
    c: InternalAlignment(g337,g340)
    c: InternalAlignment(g338,g340)
    c: InternalAlignment(g339,g340)
    c: InternalAlignment(g341,g340)
    c: InternalAlignment(g342,g340)
    c: Block(g340)
    c: Coincident(g343,g334)
    c: Horizontal(g343)
    c: Block(g343)
    c: Coincident(g344,g334)
    c: Coincident(g344,g260)
    c: Vertical(g344)
    c: Coincident(g345,g340)
    c: Coincident(g345,g254)
    c: Vertical(g345)
    c: Coincident(g347,g5)
    c: Coincident(g348,g5)
    c: Block(g346)
    c: Block(g5)
    c: Block(g348)
    c: Block(g347)
    c: Distance(g344) = 119.89
FEATURE [Sketcher::SketchObject] Sketch001
  FullyConstrained = true
  MapMode = 4
  Placement = pos=(0,0,0) rot=(0.57735,0.57735,0.57735;2.0944rad)
  Support = -> [Sketch]
  sketch-geometry (46):
    g0: BSplineCurve PolesCount=3 KnotsCount=2 Degree=2 IsPeriodic=0
    g1: ArcOfCircle CenterX=73.1223 CenterY=-32.291 CenterZ=0 NormalX=0 NormalY=0 NormalZ=1 AngleXU=0 Radius=13 StartAngle=5.92268 EndAngle=9.06428
    g2: ArcOfCircle CenterX=66.7816 CenterY=-49.1439 CenterZ=0 NormalX=0 NormalY=0 NormalZ=1 AngleXU=0 Radius=13 StartAngle=2.78068 EndAngle=5.92131
    g3: ArcOfCircle CenterX=55.9263 CenterY=-78.1807 CenterZ=0 NormalX=0 NormalY=0 NormalZ=1 AngleXU=0 Radius=13 StartAngle=5.92268 EndAngle=9.06428
    g4: ArcOfCircle CenterX=49.5884 CenterY=-95.0342 CenterZ=0 NormalX=0 NormalY=0 NormalZ=1 AngleXU=0 Radius=13 StartAngle=2.78068 EndAngle=5.92131
    g5: ArcOfCircle CenterX=38.7206 CenterY=-124.067 CenterZ=0 NormalX=0 NormalY=0 NormalZ=1 AngleXU=0 Radius=13 StartAngle=5.92268 EndAngle=9.06428
    g6: ArcOfCircle CenterX=32.3875 CenterY=-140.92 CenterZ=0 NormalX=0 NormalY=0 NormalZ=1 AngleXU=0 Radius=13 StartAngle=2.78068 EndAngle=5.92131
    g7: ArcOfCircle CenterX=21.4715 CenterY=-169.934 CenterZ=0 NormalX=0 NormalY=0 NormalZ=1 AngleXU=0 Radius=13 StartAngle=5.92268 EndAngle=9.06428
    g8: ArcOfCircle CenterX=15.1336 CenterY=-186.787 CenterZ=0 NormalX=0 NormalY=0 NormalZ=1 AngleXU=0 Radius=13 StartAngle=2.78068 EndAngle=5.92131
    g9-g12: Circle x4 (B-spline internal-alignment scaffolding for g13; pole/knot coordinates omitted)
    g13: BSplineCurve PolesCount=4 KnotsCount=2 Degree=3 IsPeriodic=0
    g14: GeomPoint X=28.8094 Y=-19.0875 Z=0
    g15: GeomPoint X=47.0443 Y=-50.4712 Z=0
    g16: Circle CenterX=53.5586 CenterY=-23.2695 CenterZ=0 NormalX=0 NormalY=0 NormalZ=1 AngleXU=0 Radius=3.24518
    g17: Circle CenterX=-195.441 CenterY=-127.082 CenterZ=0 NormalX=0 NormalY=0 NormalZ=1 AngleXU=0 Radius=1
    g18: Circle CenterX=-8.24091 CenterY=-197.481 CenterZ=0 NormalX=0 NormalY=0 NormalZ=1 AngleXU=0 Radius=1
    g19: Circle CenterX=12.8789 CenterY=-141.321 CenterZ=0 NormalX=0 NormalY=0 NormalZ=1 AngleXU=0 Radius=1
    g20: BSplineCurve PolesCount=3 KnotsCount=2 Degree=2 IsPeriodic=0
    g21: GeomPoint X=-195.441 Y=-127.082 Z=0
    g22: GeomPoint X=12.8789 Y=-141.321 Z=0
    g23: Circle CenterX=-12.8016 CenterY=-179.036 CenterZ=0 NormalX=0 NormalY=0 NormalZ=1 AngleXU=0 Radius=10.5072
    g24: Circle CenterX=0.933922 CenterY=-166.43 CenterZ=0 NormalX=0 NormalY=0 NormalZ=1 AngleXU=0 Radius=3.26661
    g25: Circle CenterX=-33.5518 CenterY=-176.44 CenterZ=0 NormalX=0 NormalY=0 NormalZ=1 AngleXU=0 Radius=5.64388
    g26: Circle CenterX=-47.2366 CenterY=-173.859 CenterZ=0 NormalX=0 NormalY=0 NormalZ=1 AngleXU=0 Radius=3.01653
    g27: Circle CenterX=-56.2595 CenterY=-171.456 CenterZ=0 NormalX=0 NormalY=0 NormalZ=1 AngleXU=0 Radius=2.12826
    g28: ArcOfCircle CenterX=51.2151 CenterY=-198.473 CenterZ=0 NormalX=0 NormalY=0 NormalZ=1 AngleXU=0 Radius=20 StartAngle=2.78189 EndAngle=4.35269
    g29: LineSegment StartX=32.4951 StartY=-191.433 StartZ=0 EndX=94.6578 EndY=-26.1352 EndZ=0
    g30: LineSegment StartX=43.1192 StartY=-220.001 StartZ=0 EndX=-196.497 EndY=-129.89 EndZ=0
    g31: LineSegment StartX=43.1192 StartY=-220.001 StartZ=0 EndX=44.1752 EndY=-217.193 EndZ=0
    g32: LineSegment StartX=117.223 StartY=-19.0875 StartZ=0 EndX=117.223 EndY=-16.0875 EndZ=0
    g33: LineSegment StartX=117.223 StartY=-16.0875 StartZ=0 EndX=17.2232 EndY=-16.0875 EndZ=0
    g34: LineSegment StartX=17.2232 StartY=-16.0875 StartZ=0 EndX=17.2232 EndY=-19.0875 EndZ=0
    g35: LineSegment StartX=28.8094 StartY=-19.0875 StartZ=0 EndX=17.2232 EndY=-19.0875 EndZ=0
    g36: LineSegment StartX=47.0443 StartY=-50.4712 StartZ=0 EndX=12.8789 EndY=-141.321 EndZ=0
    g37: LineSegment StartX=-195.441 StartY=-127.082 StartZ=0 EndX=-196.497 EndY=-129.89 EndZ=0
    g38: LineSegment StartX=85.2866 StartY=-36.8766 StartZ=0 EndX=78.9396 EndY=-53.7463 EndZ=0
    g39: LineSegment StartX=60.9579 StartY=-27.7053 StartZ=0 EndX=54.6191 EndY=-44.5532 EndZ=0
    g40: LineSegment StartX=68.0907 StartY=-82.7664 StartZ=0 EndX=61.7465 EndY=-99.6365 EndZ=0
    g41: LineSegment StartX=43.7619 StartY=-73.595 StartZ=0 EndX=37.426 EndY=-90.4435 EndZ=0
    g42: LineSegment StartX=50.885 StartY=-128.652 StartZ=0 EndX=44.5456 EndY=-145.522 EndZ=0
    g43: LineSegment StartX=26.5562 StartY=-119.481 StartZ=0 EndX=20.2251 EndY=-136.329 EndZ=0
    g44: LineSegment StartX=9.3071 StartY=-165.349 StartZ=0 EndX=2.97115 EndY=-182.197 EndZ=0
    g45: LineSegment StartX=33.6358 StartY=-174.52 StartZ=0 EndX=27.2917 EndY=-191.39 EndZ=0
  constraints (71):
    c: Block(g0)
    c: Block(g1)
    c: Block(g2)
    c: Block(g4)
    c: Block(g3)
    c: Block(g6)
    c: Block(g5)
    c: Block(g8)
    c: Block(g7)
    c: Weight(g9) = 1
    c: Equal(g9,g10)
    c: Equal(g9,g11)
    c: Equal(g9,g12)
    c: InternalAlignment(g9-g12 -> g13) x4
    c: InternalAlignment(g14,g13)
    c: InternalAlignment(g15,g13)
    c: Block(g16)
    c: Weight(g17) = 1
    c: Equal(g17,g18)
    c: Equal(g17,g19)
    c: InternalAlignment(g17,g20)
    c: InternalAlignment(g18,g20)
    c: InternalAlignment(g19,g20)
    c: InternalAlignment(g21,g20)
    c: InternalAlignment(g22,g20)
    c: Block(g20)
    c: Block(g23)
    c: Block(g24)
    c: Block(g25)
    c: Block(g26)
    c: Block(g27)
    c: Block(g28)
    c: Coincident(g29,g28)
    c: Coincident(g29,g0)
    c: Block(g13)
    c: Coincident(g31,g30)
    c: Coincident(g31,g28)
    c: Block(g31)
    c: Coincident(g32,g0)
    c: Vertical(g32)
    c: Coincident(g33,g32)
    c: Horizontal(g33)
    c: Coincident(g34,g33)
    c: Vertical(g34)
    c: Block(g33)
    c: Coincident(g35,g13)
    c: Coincident(g35,g34)
    c: Horizontal(g35)
    c: Coincident(g36,g13)
    c: Coincident(g36,g20)
    c: Coincident(g37,g20)
    c: Coincident(g37,g30)
    c: Block(g30)
    c: Coincident(g38,g1)
    c: Coincident(g38,g2)
    c: Coincident(g39,g1)
    c: Coincident(g39,g2)
    c: Coincident(g40,g3)
    c: Coincident(g40,g4)
    c: Coincident(g41,g3)
    c: Coincident(g41,g4)
    c: Coincident(g42,g5)
    c: Coincident(g42,g6)
    c: Coincident(g43,g5)
    c: Coincident(g43,g6)
    c: Coincident(g44,g7)
    c: Coincident(g44,g8)
    c: Coincident(g45,g7)
    c: Coincident(g45,g8)
    c: Distance(g30) = 256
    c: Distance(g33) = 100
FEATURE [Part::Extrusion] Extrude002
  Base = -> Sketch001
  Dir = (1,0,0)
  DirMode = 2
  FaceMakerClass = Part::FaceMakerBullseye
  LengthFwd = 8
  LengthRev = 0
  Solid = true
  Symmetric = false
FEATURE [Sketcher::SketchObject] Sketch002
  FullyConstrained = true
  sketch-geometry (20):
    g0: LineSegment StartX=-2.77179 StartY=-200.304 StartZ=0 EndX=5.22821 EndY=-200.304 EndZ=0
    g1: LineSegment StartX=5.22821 StartY=-200.304 StartZ=0 EndX=5.22821 EndY=-197.304 EndZ=0
    g2: LineSegment StartX=-2.77179 StartY=-200.304 StartZ=0 EndX=-2.77179 EndY=-197.304 EndZ=0
    g3: LineSegment StartX=5.22821 StartY=-197.304 StartZ=0 EndX=8.22821 EndY=-197.304 EndZ=0
    g4: LineSegment StartX=-2.77179 StartY=-197.304 StartZ=0 EndX=-5.77179 EndY=-197.304 EndZ=0
    g5: LineSegment StartX=19.2282 StartY=-203.304 StartZ=0 EndX=19.2282 EndY=-206.304 EndZ=0
    g6: LineSegment StartX=-16.7718 StartY=-203.304 StartZ=0 EndX=-16.7718 EndY=-206.304 EndZ=0
    g7: LineSegment StartX=-16.7718 StartY=-206.304 StartZ=0 EndX=19.2282 EndY=-206.304 EndZ=0
    g8: Circle CenterX=-16.7718 CenterY=-203.304 CenterZ=0 NormalX=0 NormalY=0 NormalZ=1 AngleXU=0 Radius=1
    g9: Circle CenterX=-5.77179 CenterY=-203.304 CenterZ=0 NormalX=0 NormalY=0 NormalZ=1 AngleXU=0 Radius=1
    g10: Circle CenterX=-5.77179 CenterY=-197.304 CenterZ=0 NormalX=0 NormalY=0 NormalZ=1 AngleXU=0 Radius=1
    g11: BSplineCurve PolesCount=3 KnotsCount=2 Degree=2 IsPeriodic=0
    g12: GeomPoint X=-16.7718 Y=-203.304 Z=0
    g13: GeomPoint X=-5.77179 Y=-197.304 Z=0
    g14: Circle CenterX=19.2282 CenterY=-203.304 CenterZ=0 NormalX=0 NormalY=0 NormalZ=1 AngleXU=0 Radius=1
    g15: Circle CenterX=8.22821 CenterY=-203.304 CenterZ=0 NormalX=0 NormalY=0 NormalZ=1 AngleXU=0 Radius=1
    g16: Circle CenterX=8.22821 CenterY=-197.304 CenterZ=0 NormalX=0 NormalY=0 NormalZ=1 AngleXU=0 Radius=1
    g17: BSplineCurve PolesCount=3 KnotsCount=2 Degree=2 IsPeriodic=0
    g18: GeomPoint X=19.2282 Y=-203.304 Z=0
    g19: GeomPoint X=8.22821 Y=-197.304 Z=0
  constraints (41):
    c: Horizontal(g0)
    c: Distance(g0) = 8
    c: Coincident(g1,g0)
    c: Vertical(g1)
    c: Distance(g1) = 3
    c: Coincident(g2,g0)
    c: Vertical(g2)
    c: Distance(g2) = 3
    c: Coincident(g3,g1)
    c: Horizontal(g3)
    c: Distance(g3) = 3
    c: Coincident(g4,g2)
    c: Horizontal(g4)
    c: Distance(g4) = 3
    c: Vertical(g5)
    c: Vertical(g6)
    c: Coincident(g7,g6)
    c: Coincident(g7,g5)
    c: Weight(g8) = 1
    c: Equal(g8,g9)
    c: Equal(g8,g10)
    c: Coincident(g11,g4)
    c: InternalAlignment(g8,g11)
    c: InternalAlignment(g9,g11)
    c: InternalAlignment(g10,g11)
    c: InternalAlignment(g12,g11)
    c: InternalAlignment(g13,g11)
    c: Coincident(g17,g5)
    c: Weight(g14) = 1
    c: Equal(g14,g15)
    c: Equal(g14,g16)
    c: Coincident(g17,g3)
    c: InternalAlignment(g14,g17)
    c: InternalAlignment(g15,g17)
    c: InternalAlignment(g16,g17)
    c: InternalAlignment(g18,g17)
    c: InternalAlignment(g19,g17)
    c: Block(g7)
    c: Block(g17)
    c: Block(g11)
    c: Block(g6)
FEATURE [Part::Extrusion] Extrude003
  Base = -> Sketch002
  Dir = (0,0,1)
  DirMode = 2
  FaceMakerClass = Part::FaceMakerBullseye
  LengthFwd = 260
  LengthRev = 0
  Solid = true
  Symmetric = false
FEATURE [Part::Extrusion] Extrude
  Base = -> Sketch
  Dir = (0,0,1)
  DirMode = 2
  FaceMakerClass = Part::FaceMakerBullseye
  LengthFwd = 14
  LengthRev = 0
  Solid = true
  Symmetric = false
FEATURE [Sketcher::SketchObject] Sketch003
  FullyConstrained = false
  sketch-geometry (357):
    g0: LineSegment StartX=-10.9272 StartY=-82.7794 StartZ=0 EndX=46.0728 EndY=-51.4823 EndZ=0
    g1: LineSegment StartX=-10.9272 StartY=76.4095 StartZ=0 EndX=-10.9272 EndY=-82.7794 EndZ=0
    g2: LineSegment StartX=46.0728 StartY=76.4095 StartZ=0 EndX=46.0728 EndY=-51.4823 EndZ=0
    g3: LineSegment StartX=-42.9272 StartY=136.221 StartZ=0 EndX=-42.9272 EndY=-103.779 EndZ=0
    g4: LineSegment StartX=407.073 StartY=136.221 StartZ=0 EndX=407.073 EndY=-103.779 EndZ=0
    g5: ArcOfCircle CenterX=-26.9272 CenterY=-83.7794 CenterZ=0 NormalX=0 NormalY=0 NormalZ=1 AngleXU=0 Radius=8 StartAngle=3.14159 EndAngle=6.28319
    g6: ArcOfCircle CenterX=391.073 CenterY=-83.7794 CenterZ=0 NormalX=0 NormalY=0 NormalZ=1 AngleXU=0 Radius=8 StartAngle=3.14159 EndAngle=6.28319
    g7: Circle CenterX=175.022 CenterY=27.0628 CenterZ=0 NormalX=0 NormalY=0 NormalZ=1 AngleXU=0 Radius=1
    g8: Circle CenterX=179.022 CenterY=24.8665 CenterZ=0 NormalX=0 NormalY=0 NormalZ=1 AngleXU=0 Radius=1
    g9: Circle CenterX=179.022 CenterY=27.0628 CenterZ=0 NormalX=0 NormalY=0 NormalZ=1 AngleXU=0 Radius=1
    g10: BSplineCurve PolesCount=3 KnotsCount=2 Degree=2 IsPeriodic=0
    g11: GeomPoint X=175.022 Y=27.0628 Z=0
    g12: GeomPoint X=179.022 Y=27.0628 Z=0
    g13: Circle CenterX=189.124 CenterY=27.0628 CenterZ=0 NormalX=0 NormalY=0 NormalZ=1 AngleXU=0 Radius=1
    g14: Circle CenterX=185.124 CenterY=24.8665 CenterZ=0 NormalX=0 NormalY=0 NormalZ=1 AngleXU=0 Radius=1
    g15: Circle CenterX=185.124 CenterY=27.0628 CenterZ=0 NormalX=0 NormalY=0 NormalZ=1 AngleXU=0 Radius=1
    g16: BSplineCurve PolesCount=3 KnotsCount=2 Degree=2 IsPeriodic=0
    g17: GeomPoint X=189.124 Y=27.0628 Z=0
    g18: GeomPoint X=185.124 Y=27.0628 Z=0
    g19: Circle CenterX=175.022 CenterY=5.37834 CenterZ=0 NormalX=0 NormalY=0 NormalZ=1 AngleXU=0 Radius=1
    g20: Circle CenterX=179.022 CenterY=7.57463 CenterZ=0 NormalX=0 NormalY=0 NormalZ=1 AngleXU=0 Radius=1
    g21: Circle CenterX=179.022 CenterY=5.34704 CenterZ=0 NormalX=0 NormalY=0 NormalZ=1 AngleXU=0 Radius=1
    g22: BSplineCurve PolesCount=3 KnotsCount=2 Degree=2 IsPeriodic=0
    g23: GeomPoint X=175.022 Y=5.37834 Z=0
    g24: GeomPoint X=179.022 Y=5.34704 Z=0
    g25: Circle CenterX=189.124 CenterY=5.37834 CenterZ=0 NormalX=0 NormalY=0 NormalZ=1 AngleXU=0 Radius=1
    g26: Circle CenterX=185.124 CenterY=7.57463 CenterZ=0 NormalX=0 NormalY=0 NormalZ=1 AngleXU=0 Radius=1
    g27: Circle CenterX=185.124 CenterY=5.34704 CenterZ=0 NormalX=0 NormalY=0 NormalZ=1 AngleXU=0 Radius=1
    g28: BSplineCurve PolesCount=3 KnotsCount=2 Degree=2 IsPeriodic=0
    g29: GeomPoint X=189.124 Y=5.37834 Z=0
    g30: GeomPoint X=185.124 Y=5.34704 Z=0
    g31: Circle CenterX=165.871 CenterY=18.1458 CenterZ=0 NormalX=0 NormalY=0 NormalZ=1 AngleXU=0 Radius=1
    g32: Circle CenterX=169.377 CenterY=16.2206 CenterZ=0 NormalX=0 NormalY=0 NormalZ=1 AngleXU=0 Radius=1
    g33: Circle CenterX=165.871 CenterY=14.2954 CenterZ=0 NormalX=0 NormalY=0 NormalZ=1 AngleXU=0 Radius=1
    g34: BSplineCurve PolesCount=3 KnotsCount=2 Degree=2 IsPeriodic=0
    g35: GeomPoint X=165.871 Y=18.1458 Z=0
    g36: GeomPoint X=165.871 Y=14.2954 Z=0
    g37: Circle CenterX=198.275 CenterY=18.1458 CenterZ=0 NormalX=0 NormalY=0 NormalZ=1 AngleXU=0 Radius=1
    g38: Circle CenterX=194.768 CenterY=16.2206 CenterZ=0 NormalX=0 NormalY=0 NormalZ=1 AngleXU=0 Radius=1
    g39: Circle CenterX=198.275 CenterY=14.2954 CenterZ=0 NormalX=0 NormalY=0 NormalZ=1 AngleXU=0 Radius=1
    g40: BSplineCurve PolesCount=3 KnotsCount=2 Degree=2 IsPeriodic=0
    g41: GeomPoint X=198.275 Y=18.1458 Z=0
    g42: GeomPoint X=198.275 Y=14.2954 Z=0
    g43: LineSegment StartX=407.073 StartY=-103.779 StartZ=0 EndX=-42.9272 EndY=-103.779 EndZ=0
    g44: LineSegment StartX=407.073 StartY=136.221 StartZ=0 EndX=-42.9272 EndY=136.221 EndZ=0
    g45: LineSegment StartX=46.0728 StartY=76.4095 StartZ=0 EndX=-10.9272 EndY=76.4095 EndZ=0
    g46: Circle CenterX=125.607 CenterY=54.1951 CenterZ=0 NormalX=0 NormalY=0 NormalZ=1 AngleXU=0 Radius=1
    g47: Circle CenterX=139.632 CenterY=46.4944 CenterZ=0 NormalX=0 NormalY=0 NormalZ=1 AngleXU=0 Radius=1
    g48: Circle CenterX=127.326 CenterY=56.7187 CenterZ=0 NormalX=0 NormalY=0 NormalZ=1 AngleXU=0 Radius=1
    g49: BSplineCurve PolesCount=3 KnotsCount=2 Degree=2 IsPeriodic=0
    g50: GeomPoint X=125.607 Y=54.1951 Z=0
    g51: GeomPoint X=127.326 Y=56.7187 Z=0
    g52: Circle CenterX=236.821 CenterY=56.7187 CenterZ=0 NormalX=0 NormalY=0 NormalZ=1 AngleXU=0 Radius=1
    g53: Circle CenterX=224.513 CenterY=46.4944 CenterZ=0 NormalX=0 NormalY=0 NormalZ=1 AngleXU=0 Radius=1
    g54: Circle CenterX=238.538 CenterY=54.1951 CenterZ=0 NormalX=0 NormalY=0 NormalZ=1 AngleXU=0 Radius=1
    g55: BSplineCurve PolesCount=3 KnotsCount=2 Degree=2 IsPeriodic=0
    g56: GeomPoint X=236.821 Y=56.7187 Z=0
    g57: GeomPoint X=238.538 Y=54.1951 Z=0
    g58: Circle CenterX=238.538 CenterY=-21.7539 CenterZ=0 NormalX=0 NormalY=0 NormalZ=1 AngleXU=0 Radius=1
    g59: Circle CenterX=224.513 CenterY=-14.0532 CenterZ=0 NormalX=0 NormalY=0 NormalZ=1 AngleXU=0 Radius=1
    g60: Circle CenterX=236.821 CenterY=-24.2775 CenterZ=0 NormalX=0 NormalY=0 NormalZ=1 AngleXU=0 Radius=1
    g61: BSplineCurve PolesCount=3 KnotsCount=2 Degree=2 IsPeriodic=0
    g62: GeomPoint X=238.538 Y=-21.7539 Z=0
    g63: GeomPoint X=236.821 Y=-24.2775 Z=0
    g64: Circle CenterX=125.607 CenterY=-21.7539 CenterZ=0 NormalX=0 NormalY=0 NormalZ=1 AngleXU=0 Radius=1
    g65: Circle CenterX=139.632 CenterY=-14.0532 CenterZ=0 NormalX=0 NormalY=0 NormalZ=1 AngleXU=0 Radius=1
    g66: Circle CenterX=127.325 CenterY=-24.2775 CenterZ=0 NormalX=0 NormalY=0 NormalZ=1 AngleXU=0 Radius=1
    g67: BSplineCurve PolesCount=3 KnotsCount=2 Degree=2 IsPeriodic=0
    g68: GeomPoint X=125.607 Y=-21.7539 Z=0
    g69: GeomPoint X=127.325 Y=-24.2775 Z=0
    g70: Circle CenterX=302.996 CenterY=111.695 CenterZ=0 NormalX=0 NormalY=0 NormalZ=1 AngleXU=0 Radius=1
    g71: Circle CenterX=306.073 CenterY=114.251 CenterZ=0 NormalX=0 NormalY=0 NormalZ=1 AngleXU=0 Radius=1
    g72: Circle CenterX=306.073 CenterY=110.251 CenterZ=0 NormalX=0 NormalY=0 NormalZ=1 AngleXU=0 Radius=1
    g73: BSplineCurve PolesCount=3 KnotsCount=2 Degree=2 IsPeriodic=0
    g74: GeomPoint X=302.996 Y=111.695 Z=0
    g75: GeomPoint X=306.073 Y=110.251 Z=0
    g76: Circle CenterX=306.073 CenterY=95.2763 CenterZ=0 NormalX=0 NormalY=0 NormalZ=1 AngleXU=0 Radius=1
    g77: Circle CenterX=306.073 CenterY=91.2763 CenterZ=0 NormalX=0 NormalY=0 NormalZ=1 AngleXU=0 Radius=1
    g78: Circle CenterX=302.567 CenterY=89.3511 CenterZ=0 NormalX=0 NormalY=0 NormalZ=1 AngleXU=0 Radius=1
    g79: BSplineCurve PolesCount=3 KnotsCount=2 Degree=2 IsPeriodic=0
    g80: GeomPoint X=306.073 Y=95.2763 Z=0
    g81: GeomPoint X=302.567 Y=89.3511 Z=0
    g82: LineSegment StartX=306.073 StartY=110.251 StartZ=0 EndX=306.073 EndY=95.2763 EndZ=0
    g83: LineSegment StartX=302.996 StartY=111.695 StartZ=0 EndX=236.821 EndY=56.7187 EndZ=0
    g84: LineSegment StartX=238.538 StartY=54.1951 StartZ=0 EndX=302.567 EndY=89.3511 EndZ=0
    g85: Circle CenterX=61.1496 CenterY=111.695 CenterZ=0 NormalX=0 NormalY=0 NormalZ=1 AngleXU=0 Radius=1
    g86: Circle CenterX=58.0728 CenterY=114.251 CenterZ=0 NormalX=0 NormalY=0 NormalZ=1 AngleXU=0 Radius=1
    g87: Circle CenterX=58.0728 CenterY=110.251 CenterZ=0 NormalX=0 NormalY=0 NormalZ=1 AngleXU=0 Radius=1
    g88: BSplineCurve PolesCount=3 KnotsCount=2 Degree=2 IsPeriodic=0
    g89: GeomPoint X=61.1496 Y=111.695 Z=0
    g90: GeomPoint X=58.0728 Y=110.251 Z=0
    g91: Circle CenterX=61.5791 CenterY=89.3511 CenterZ=0 NormalX=0 NormalY=0 NormalZ=1 AngleXU=0 Radius=1
    g92: Circle CenterX=58.0728 CenterY=91.2763 CenterZ=0 NormalX=0 NormalY=0 NormalZ=1 AngleXU=0 Radius=1
    g93: Circle CenterX=58.0728 CenterY=95.2763 CenterZ=0 NormalX=0 NormalY=0 NormalZ=1 AngleXU=0 Radius=1
    g94: BSplineCurve PolesCount=3 KnotsCount=2 Degree=2 IsPeriodic=0
    g95: GeomPoint X=61.5791 Y=89.3511 Z=0
    g96: GeomPoint X=58.0728 Y=95.2763 Z=0
    g97: LineSegment StartX=58.0728 StartY=110.251 StartZ=0 EndX=58.0728 EndY=95.2763 EndZ=0
    g98: LineSegment StartX=61.1496 StartY=111.695 StartZ=0 EndX=127.326 EndY=56.7187 EndZ=0
    g99: LineSegment StartX=125.607 StartY=54.1951 StartZ=0 EndX=61.5791 EndY=89.3511 EndZ=0
    g100: Circle CenterX=61.5791 CenterY=-56.9099 CenterZ=0 NormalX=0 NormalY=0 NormalZ=1 AngleXU=0 Radius=1
    g101: Circle CenterX=58.0728 CenterY=-58.8351 CenterZ=0 NormalX=0 NormalY=0 NormalZ=1 AngleXU=0 Radius=1
    g102: Circle CenterX=58.0728 CenterY=-62.8351 CenterZ=0 NormalX=0 NormalY=0 NormalZ=1 AngleXU=0 Radius=1
    g103: BSplineCurve PolesCount=3 KnotsCount=2 Degree=2 IsPeriodic=0
    g104: GeomPoint X=61.5791 Y=-56.9099 Z=0
    g105: GeomPoint X=58.0728 Y=-62.8351 Z=0
    g106: Circle CenterX=58.0728 CenterY=-77.8102 CenterZ=0 NormalX=0 NormalY=0 NormalZ=1 AngleXU=0 Radius=1
    g107: Circle CenterX=58.0728 CenterY=-81.8102 CenterZ=0 NormalX=0 NormalY=0 NormalZ=1 AngleXU=0 Radius=1
    g108: Circle CenterX=61.1496 CenterY=-79.2541 CenterZ=0 NormalX=0 NormalY=0 NormalZ=1 AngleXU=0 Radius=1
    g109: BSplineCurve PolesCount=3 KnotsCount=2 Degree=2 IsPeriodic=0
    g110: GeomPoint X=58.0728 Y=-77.8102 Z=0
    g111: GeomPoint X=61.1496 Y=-79.2541 Z=0
    g112: LineSegment StartX=58.0728 StartY=-62.8351 StartZ=0 EndX=58.0728 EndY=-77.8102 EndZ=0
    g113: LineSegment StartX=61.1496 StartY=-79.2541 StartZ=0 EndX=127.325 EndY=-24.2775 EndZ=0
    g114: LineSegment StartX=125.607 StartY=-21.7539 StartZ=0 EndX=61.5791 EndY=-56.9099 EndZ=0
    g115: Circle CenterX=302.567 CenterY=-56.9099 CenterZ=0 NormalX=0 NormalY=0 NormalZ=1 AngleXU=0 Radius=1
    g116: Circle CenterX=306.073 CenterY=-58.8351 CenterZ=0 NormalX=0 NormalY=0 NormalZ=1 AngleXU=0 Radius=1
    g117: Circle CenterX=306.073 CenterY=-62.8351 CenterZ=0 NormalX=0 NormalY=0 NormalZ=1 AngleXU=0 Radius=1
    g118: BSplineCurve PolesCount=3 KnotsCount=2 Degree=2 IsPeriodic=0
    g119: GeomPoint X=302.567 Y=-56.9099 Z=0
    g120: GeomPoint X=306.073 Y=-62.8351 Z=0
    g121: Circle CenterX=302.996 CenterY=-79.2541 CenterZ=0 NormalX=0 NormalY=0 NormalZ=1 AngleXU=0 Radius=1
    g122: Circle CenterX=306.073 CenterY=-81.8102 CenterZ=0 NormalX=0 NormalY=0 NormalZ=1 AngleXU=0 Radius=1
    g123: Circle CenterX=306.073 CenterY=-77.8102 CenterZ=0 NormalX=0 NormalY=0 NormalZ=1 AngleXU=0 Radius=1
    g124: BSplineCurve PolesCount=3 KnotsCount=2 Degree=2 IsPeriodic=0
    g125: GeomPoint X=302.996 Y=-79.2541 Z=0
    g126: GeomPoint X=306.073 Y=-77.8102 Z=0
    g127: LineSegment StartX=306.073 StartY=-62.8351 StartZ=0 EndX=306.073 EndY=-77.8102 EndZ=0
    g128: LineSegment StartX=302.996 StartY=-79.2541 StartZ=0 EndX=236.821 EndY=-24.2775 EndZ=0
    g129: LineSegment StartX=238.538 StartY=-21.7539 StartZ=0 EndX=302.567 EndY=-56.9099 EndZ=0
    g130: Circle CenterX=61.6457 CenterY=-88.8112 CenterZ=0 NormalX=0 NormalY=0 NormalZ=1 AngleXU=0 Radius=1
    g131: Circle CenterX=58.0728 CenterY=-91.7794 CenterZ=0 NormalX=0 NormalY=0 NormalZ=1 AngleXU=0 Radius=1
    g132: Circle CenterX=63.9135 CenterY=-91.7794 CenterZ=0 NormalX=0 NormalY=0 NormalZ=1 AngleXU=0 Radius=1
    g133: BSplineCurve PolesCount=3 KnotsCount=2 Degree=2 IsPeriodic=0
    g134: GeomPoint X=61.6457 Y=-88.8112 Z=0
    g135: GeomPoint X=63.9135 Y=-91.7794 Z=0
    g136: Circle CenterX=179.022 CenterY=-85.8163 CenterZ=0 NormalX=0 NormalY=0 NormalZ=1 AngleXU=0 Radius=1
    g137: Circle CenterX=179.022 CenterY=-91.7794 CenterZ=0 NormalX=0 NormalY=0 NormalZ=1 AngleXU=0 Radius=1
    g138: Circle CenterX=171.895 CenterY=-91.7794 CenterZ=0 NormalX=0 NormalY=0 NormalZ=1 AngleXU=0 Radius=1
    g139: BSplineCurve PolesCount=3 KnotsCount=2 Degree=2 IsPeriodic=0
    g140: GeomPoint X=179.022 Y=-85.8163 Z=0
    g141: GeomPoint X=171.895 Y=-91.7794 Z=0
    g142: Circle CenterX=185.124 CenterY=-86.2028 CenterZ=0 NormalX=0 NormalY=0 NormalZ=1 AngleXU=0 Radius=1
    g143: Circle CenterX=185.124 CenterY=-91.7794 CenterZ=0 NormalX=0 NormalY=0 NormalZ=1 AngleXU=0 Radius=1
    g144: Circle CenterX=191.747 CenterY=-91.7794 CenterZ=0 NormalX=0 NormalY=0 NormalZ=1 AngleXU=0 Radius=1
    g145: BSplineCurve PolesCount=3 KnotsCount=2 Degree=2 IsPeriodic=0
    g146: GeomPoint X=185.124 Y=-86.2028 Z=0
    g147: GeomPoint X=191.747 Y=-91.7794 Z=0
    g148: Circle CenterX=299.888 CenterY=-86.6413 CenterZ=0 NormalX=0 NormalY=0 NormalZ=1 AngleXU=0 Radius=1
    g149: Circle CenterX=306.073 CenterY=-91.7794 CenterZ=0 NormalX=0 NormalY=0 NormalZ=1 AngleXU=0 Radius=1
    g150: Circle CenterX=298.776 CenterY=-91.7794 CenterZ=0 NormalX=0 NormalY=0 NormalZ=1 AngleXU=0 Radius=1
    g151: BSplineCurve PolesCount=3 KnotsCount=2 Degree=2 IsPeriodic=0
    g152: GeomPoint X=299.888 Y=-86.6413 Z=0
    g153: GeomPoint X=298.776 Y=-91.7794 Z=0
    g154: LineSegment StartX=189.124 StartY=5.37834 StartZ=0 EndX=299.888 EndY=-86.6413 EndZ=0
    g155: LineSegment StartX=298.776 StartY=-91.7794 StartZ=0 EndX=191.747 EndY=-91.7794 EndZ=0
    g156: LineSegment StartX=185.124 StartY=-86.2028 StartZ=0 EndX=185.124 EndY=5.34704 EndZ=0
    g157: LineSegment StartX=179.022 StartY=5.34704 StartZ=0 EndX=179.022 EndY=-85.8163 EndZ=0
    g158: LineSegment StartX=171.895 StartY=-91.7794 StartZ=0 EndX=63.9135 EndY=-91.7794 EndZ=0
    g159: LineSegment StartX=61.6457 StartY=-88.8112 StartZ=0 EndX=175.022 EndY=5.37834 EndZ=0
    g160: Circle CenterX=302.073 CenterY=124.221 CenterZ=0 NormalX=0 NormalY=0 NormalZ=1 AngleXU=0 Radius=1
    g161: Circle CenterX=306.073 CenterY=124.221 CenterZ=0 NormalX=0 NormalY=0 NormalZ=1 AngleXU=0 Radius=1
    g162: Circle CenterX=302.996 CenterY=121.665 CenterZ=0 NormalX=0 NormalY=0 NormalZ=1 AngleXU=0 Radius=1
    g163: BSplineCurve PolesCount=3 KnotsCount=2 Degree=2 IsPeriodic=0
    g164: GeomPoint X=302.073 Y=124.221 Z=0
    g165: GeomPoint X=302.996 Y=121.665 Z=0
    g166: Circle CenterX=189.124 CenterY=124.221 CenterZ=0 NormalX=0 NormalY=0 NormalZ=1 AngleXU=0 Radius=1
    g167: Circle CenterX=185.124 CenterY=124.221 CenterZ=0 NormalX=0 NormalY=0 NormalZ=1 AngleXU=0 Radius=1
    g168: Circle CenterX=185.124 CenterY=120.221 CenterZ=0 NormalX=0 NormalY=0 NormalZ=1 AngleXU=0 Radius=1
    g169: BSplineCurve PolesCount=3 KnotsCount=2 Degree=2 IsPeriodic=0
    g170: GeomPoint X=189.124 Y=124.221 Z=0
    g171: GeomPoint X=185.124 Y=120.221 Z=0
    g172: Circle CenterX=175.022 CenterY=124.221 CenterZ=0 NormalX=0 NormalY=0 NormalZ=1 AngleXU=0 Radius=1
    g173: Circle CenterX=179.022 CenterY=124.221 CenterZ=0 NormalX=0 NormalY=0 NormalZ=1 AngleXU=0 Radius=1
    g174: Circle CenterX=179.022 CenterY=120.221 CenterZ=0 NormalX=0 NormalY=0 NormalZ=1 AngleXU=0 Radius=1
    g175: BSplineCurve PolesCount=3 KnotsCount=2 Degree=2 IsPeriodic=0
    g176: GeomPoint X=175.022 Y=124.221 Z=0
    g177: GeomPoint X=179.022 Y=120.221 Z=0
    g178: Circle CenterX=62.0728 CenterY=124.221 CenterZ=0 NormalX=0 NormalY=0 NormalZ=1 AngleXU=0 Radius=1
    g179: Circle CenterX=58.0728 CenterY=124.221 CenterZ=0 NormalX=0 NormalY=0 NormalZ=1 AngleXU=0 Radius=1
    g180: Circle CenterX=61.1496 CenterY=121.665 CenterZ=0 NormalX=0 NormalY=0 NormalZ=1 AngleXU=0 Radius=1
    g181: BSplineCurve PolesCount=3 KnotsCount=2 Degree=2 IsPeriodic=0
    g182: GeomPoint X=62.0728 Y=124.221 Z=0
    g183: GeomPoint X=61.1496 Y=121.665 Z=0
    g184: LineSegment StartX=62.0728 StartY=124.221 StartZ=0 EndX=175.022 EndY=124.221 EndZ=0
    g185: LineSegment StartX=179.022 StartY=120.221 StartZ=0 EndX=179.022 EndY=27.0628 EndZ=0
    g186: LineSegment StartX=185.124 StartY=27.0628 StartZ=0 EndX=185.124 EndY=120.221 EndZ=0
    g187: LineSegment StartX=189.124 StartY=124.221 StartZ=0 EndX=302.073 EndY=124.221 EndZ=0
    g188: LineSegment StartX=302.996 StartY=121.665 StartZ=0 EndX=189.124 EndY=27.0628 EndZ=0
    g189: LineSegment StartX=175.022 StartY=27.0628 StartZ=0 EndX=61.1496 EndY=121.665 EndZ=0
    g190: Circle CenterX=61.5791 CenterY=75.4095 CenterZ=0 NormalX=0 NormalY=0 NormalZ=1 AngleXU=0 Radius=1
    g191: Circle CenterX=58.0728 CenterY=77.3346 CenterZ=0 NormalX=0 NormalY=0 NormalZ=1 AngleXU=0 Radius=1
    g192: Circle CenterX=58.0728 CenterY=73.3346 CenterZ=0 NormalX=0 NormalY=0 NormalZ=1 AngleXU=0 Radius=1
    g193: BSplineCurve PolesCount=3 KnotsCount=2 Degree=2 IsPeriodic=0
    g194: GeomPoint X=61.5791 Y=75.4095 Z=0
    g195: GeomPoint X=58.0728 Y=73.3346 Z=0
    g196: Circle CenterX=58.0728 CenterY=-40.8935 CenterZ=0 NormalX=0 NormalY=0 NormalZ=1 AngleXU=0 Radius=1
    g197: Circle CenterX=58.0728 CenterY=-44.8935 CenterZ=0 NormalX=0 NormalY=0 NormalZ=1 AngleXU=0 Radius=1
    g198: Circle CenterX=61.5791 CenterY=-42.9683 CenterZ=0 NormalX=0 NormalY=0 NormalZ=1 AngleXU=0 Radius=1
    g199: BSplineCurve PolesCount=3 KnotsCount=2 Degree=2 IsPeriodic=0
    g200: GeomPoint X=58.0728 Y=-40.8935 Z=0
    g201: GeomPoint X=61.5791 Y=-42.9683 Z=0
    g202: LineSegment StartX=61.5791 StartY=-42.9683 StartZ=0 EndX=165.871 EndY=14.2954 EndZ=0
    g203: LineSegment StartX=165.871 StartY=18.1458 StartZ=0 EndX=61.5791 EndY=75.4095 EndZ=0
    g204: LineSegment StartX=58.0728 StartY=73.3346 StartZ=0 EndX=58.0728 EndY=-40.8935 EndZ=0
    g205: Circle CenterX=302.567 CenterY=-42.9683 CenterZ=0 NormalX=0 NormalY=0 NormalZ=1 AngleXU=0 Radius=1
    g206: Circle CenterX=306.073 CenterY=-44.8935 CenterZ=0 NormalX=0 NormalY=0 NormalZ=1 AngleXU=0 Radius=1
    g207: Circle CenterX=306.073 CenterY=-40.8935 CenterZ=0 NormalX=0 NormalY=0 NormalZ=1 AngleXU=0 Radius=1
    g208: BSplineCurve PolesCount=3 KnotsCount=2 Degree=2 IsPeriodic=0
    g209: GeomPoint X=302.567 Y=-42.9683 Z=0
    g210: GeomPoint X=306.073 Y=-40.8935 Z=0
    g211: Circle CenterX=306.073 CenterY=73.3346 CenterZ=0 NormalX=0 NormalY=0 NormalZ=1 AngleXU=0 Radius=1
    g212: Circle CenterX=306.073 CenterY=77.3346 CenterZ=0 NormalX=0 NormalY=0 NormalZ=1 AngleXU=0 Radius=1
    g213: Circle CenterX=302.567 CenterY=75.4095 CenterZ=0 NormalX=0 NormalY=0 NormalZ=1 AngleXU=0 Radius=1
    g214: BSplineCurve PolesCount=3 KnotsCount=2 Degree=2 IsPeriodic=0
    g215: GeomPoint X=306.073 Y=73.3346 Z=0
    g216: GeomPoint X=302.567 Y=75.4095 Z=0
    g217: LineSegment StartX=302.567 StartY=-42.9683 StartZ=0 EndX=198.275 EndY=14.2954 EndZ=0
    g218: LineSegment StartX=198.275 StartY=18.1458 StartZ=0 EndX=302.567 EndY=75.4095 EndZ=0
    g219: LineSegment StartX=306.073 StartY=73.3346 StartZ=0 EndX=306.073 EndY=-40.8935 EndZ=0
    g220: LineSegment StartX=322.073 StartY=105.865 StartZ=0 EndX=328.643 EndY=105.865 EndZ=0
    g221: LineSegment StartX=318.073 StartY=120.221 StartZ=0 EndX=318.073 EndY=109.865 EndZ=0
    g222: LineSegment StartX=336.157 StartY=107.779 StartZ=0 EndX=362.567 EndY=122.294 EndZ=0
    g223: Circle CenterX=362.073 CenterY=124.221 CenterZ=0 NormalX=0 NormalY=0 NormalZ=1 AngleXU=0 Radius=1
    g224: Circle CenterX=366.073 CenterY=124.221 CenterZ=0 NormalX=0 NormalY=0 NormalZ=1 AngleXU=0 Radius=1
    g225: Circle CenterX=362.567 CenterY=122.294 CenterZ=0 NormalX=0 NormalY=0 NormalZ=1 AngleXU=0 Radius=1
    g226: BSplineCurve PolesCount=3 KnotsCount=2 Degree=2 IsPeriodic=0
    g227: GeomPoint X=362.073 Y=124.221 Z=0
    g228: GeomPoint X=362.567 Y=122.294 Z=0
    g229: Circle CenterX=322.073 CenterY=124.221 CenterZ=0 NormalX=0 NormalY=0 NormalZ=1 AngleXU=0 Radius=1
    g230: Circle CenterX=318.073 CenterY=124.221 CenterZ=0 NormalX=0 NormalY=0 NormalZ=1 AngleXU=0 Radius=1
    g231: Circle CenterX=318.073 CenterY=120.221 CenterZ=0 NormalX=0 NormalY=0 NormalZ=1 AngleXU=0 Radius=1
    g232: BSplineCurve PolesCount=3 KnotsCount=2 Degree=2 IsPeriodic=0
    g233: GeomPoint X=322.073 Y=124.221 Z=0
    g234: GeomPoint X=318.073 Y=120.221 Z=0
    g235: Circle CenterX=322.073 CenterY=105.865 CenterZ=0 NormalX=0 NormalY=0 NormalZ=1 AngleXU=0 Radius=1
    g236: Circle CenterX=318.073 CenterY=105.865 CenterZ=0 NormalX=0 NormalY=0 NormalZ=1 AngleXU=0 Radius=1
    g237: Circle CenterX=318.073 CenterY=109.865 CenterZ=0 NormalX=0 NormalY=0 NormalZ=1 AngleXU=0 Radius=1
    g238: BSplineCurve PolesCount=3 KnotsCount=2 Degree=2 IsPeriodic=0
    g239: GeomPoint X=322.073 Y=105.865 Z=0
    g240: GeomPoint X=318.073 Y=109.865 Z=0
    g241: Circle CenterX=336.157 CenterY=107.779 CenterZ=0 NormalX=0 NormalY=0 NormalZ=1 AngleXU=0 Radius=1
    g242: Circle CenterX=332.651 CenterY=105.853 CenterZ=0 NormalX=0 NormalY=0 NormalZ=1 AngleXU=0 Radius=1
    g243: Circle CenterX=328.643 CenterY=105.865 CenterZ=0 NormalX=0 NormalY=0 NormalZ=1 AngleXU=0 Radius=1
    g244: BSplineCurve PolesCount=3 KnotsCount=2 Degree=2 IsPeriodic=0
    g245: GeomPoint X=336.157 Y=107.779 Z=0
    g246: GeomPoint X=328.643 Y=105.865 Z=0
    g247: LineSegment StartX=322.073 StartY=124.221 StartZ=0 EndX=362.073 EndY=124.221 EndZ=0
    g248: Circle CenterX=371.567 CenterY=-80.8644 CenterZ=0 NormalX=0 NormalY=0 NormalZ=1 AngleXU=0 Radius=1
    g249: Circle CenterX=375.073 CenterY=-82.7896 CenterZ=0 NormalX=0 NormalY=0 NormalZ=1 AngleXU=0 Radius=1
    g250: Circle CenterX=375.073 CenterY=-78.7896 CenterZ=0 NormalX=0 NormalY=0 NormalZ=1 AngleXU=0 Radius=1
    g251: BSplineCurve PolesCount=3 KnotsCount=2 Degree=2 IsPeriodic=0
    g252: GeomPoint X=371.567 Y=-80.8644 Z=0
    g253: GeomPoint X=375.073 Y=-78.7896 Z=0
    g254: Circle CenterX=321.579 CenterY=-53.4075 CenterZ=0 NormalX=0 NormalY=0 NormalZ=1 AngleXU=0 Radius=1
    g255: Circle CenterX=318.073 CenterY=-51.4823 CenterZ=0 NormalX=0 NormalY=0 NormalZ=1 AngleXU=0 Radius=1
    g256: Circle CenterX=318.073 CenterY=-47.4805 CenterZ=0 NormalX=0 NormalY=0 NormalZ=1 AngleXU=0 Radius=1
    g257: BSplineCurve PolesCount=3 KnotsCount=2 Degree=2 IsPeriodic=0
    g258: GeomPoint X=321.579 Y=-53.4075 Z=0
    g259: GeomPoint X=318.073 Y=-47.4805 Z=0
    g260: LineSegment StartX=371.567 StartY=-80.8644 StartZ=0 EndX=321.579 EndY=-53.4075 EndZ=0
    g261: Circle CenterX=321.579 CenterY=-67.3492 CenterZ=0 NormalX=0 NormalY=0 NormalZ=1 AngleXU=0 Radius=1
    g262: Circle CenterX=318.073 CenterY=-65.424 CenterZ=0 NormalX=0 NormalY=0 NormalZ=1 AngleXU=0 Radius=1
    g263: Circle CenterX=318.073 CenterY=-69.424 CenterZ=0 NormalX=0 NormalY=0 NormalZ=1 AngleXU=0 Radius=1
    g264: BSplineCurve PolesCount=3 KnotsCount=2 Degree=2 IsPeriodic=0
    g265: GeomPoint X=321.579 Y=-67.3492 Z=0
    g266: GeomPoint X=318.073 Y=-69.424 Z=0
    g267: Circle CenterX=362.567 CenterY=-89.8542 CenterZ=0 NormalX=0 NormalY=0 NormalZ=1 AngleXU=0 Radius=1
    g268: Circle CenterX=366.073 CenterY=-91.7794 CenterZ=0 NormalX=0 NormalY=0 NormalZ=1 AngleXU=0 Radius=1
    g269: Circle CenterX=362.073 CenterY=-91.7794 CenterZ=0 NormalX=0 NormalY=0 NormalZ=1 AngleXU=0 Radius=1
    g270: BSplineCurve PolesCount=3 KnotsCount=2 Degree=2 IsPeriodic=0
    g271: GeomPoint X=362.567 Y=-89.8542 Z=0
    g272: GeomPoint X=362.073 Y=-91.7794 Z=0
    g273: Circle CenterX=322.073 CenterY=-91.7794 CenterZ=0 NormalX=0 NormalY=0 NormalZ=1 AngleXU=0 Radius=1
    g274: Circle CenterX=318.073 CenterY=-91.7794 CenterZ=0 NormalX=0 NormalY=0 NormalZ=1 AngleXU=0 Radius=1
    g275: Circle CenterX=318.073 CenterY=-87.7794 CenterZ=0 NormalX=0 NormalY=0 NormalZ=1 AngleXU=0 Radius=1
    g276: BSplineCurve PolesCount=3 KnotsCount=2 Degree=2 IsPeriodic=0
    g277: GeomPoint X=322.073 Y=-91.7794 Z=0
    g278: GeomPoint X=318.073 Y=-87.7794 Z=0
    g279: LineSegment StartX=362.567 StartY=-89.8542 StartZ=0 EndX=321.579 EndY=-67.3492 EndZ=0
    g280: LineSegment StartX=318.073 StartY=-69.424 StartZ=0 EndX=318.073 EndY=-87.7794 EndZ=0
    g281: LineSegment StartX=322.073 StartY=-91.7794 StartZ=0 EndX=362.073 EndY=-91.7794 EndZ=0
    g282: Circle CenterX=2.07281 CenterY=124.221 CenterZ=0 NormalX=0 NormalY=0 NormalZ=1 AngleXU=0 Radius=1
    g283: Circle CenterX=1.57905 CenterY=122.295 CenterZ=0 NormalX=0 NormalY=0 NormalZ=1 AngleXU=0 Radius=1
    g284: BSplineCurve PolesCount=3 KnotsCount=2 Degree=2 IsPeriodic=0
    g285: GeomPoint X=2.07281 Y=124.221 Z=0
    g286: GeomPoint X=1.57905 Y=122.295 Z=0
    g287: Circle CenterX=42.0728 CenterY=124.221 CenterZ=0 NormalX=0 NormalY=0 NormalZ=1 AngleXU=0 Radius=1
    g288: Circle CenterX=46.0728 CenterY=124.221 CenterZ=0 NormalX=0 NormalY=0 NormalZ=1 AngleXU=0 Radius=1
    g289: Circle CenterX=46.0728 CenterY=120.221 CenterZ=0 NormalX=0 NormalY=0 NormalZ=1 AngleXU=0 Radius=1
    g290: BSplineCurve PolesCount=3 KnotsCount=2 Degree=2 IsPeriodic=0
    g291: GeomPoint X=42.0728 Y=124.221 Z=0
    g292: GeomPoint X=46.0728 Y=120.221 Z=0
    g293: Circle CenterX=46.0728 CenterY=109.865 CenterZ=0 NormalX=0 NormalY=0 NormalZ=1 AngleXU=0 Radius=1
    g294: Circle CenterX=46.0728 CenterY=105.865 CenterZ=0 NormalX=0 NormalY=0 NormalZ=1 AngleXU=0 Radius=1
    g295: Circle CenterX=42.0728 CenterY=105.865 CenterZ=0 NormalX=0 NormalY=0 NormalZ=1 AngleXU=0 Radius=1
    g296: BSplineCurve PolesCount=3 KnotsCount=2 Degree=2 IsPeriodic=0
    g297: GeomPoint X=46.0728 Y=109.865 Z=0
    g298: GeomPoint X=42.0728 Y=105.865 Z=0
    g299: Circle CenterX=35.5028 CenterY=105.865 CenterZ=0 NormalX=0 NormalY=0 NormalZ=1 AngleXU=0 Radius=1
    g300: Circle CenterX=31.5028 CenterY=105.865 CenterZ=0 NormalX=0 NormalY=0 NormalZ=1 AngleXU=0 Radius=1
    g301: Circle CenterX=27.9965 CenterY=107.79 CenterZ=0 NormalX=0 NormalY=0 NormalZ=1 AngleXU=0 Radius=1
    g302: BSplineCurve PolesCount=3 KnotsCount=2 Degree=2 IsPeriodic=0
    g303: GeomPoint X=35.5028 Y=105.865 Z=0
    g304: GeomPoint X=27.9965 Y=107.79 Z=0
    g305: LineSegment StartX=2.07281 StartY=124.221 StartZ=0 EndX=42.0728 EndY=124.221 EndZ=0
    g306: LineSegment StartX=46.0728 StartY=120.221 StartZ=0 EndX=46.0728 EndY=109.865 EndZ=0
    g307: LineSegment StartX=42.0728 StartY=105.865 StartZ=0 EndX=35.5028 EndY=105.865 EndZ=0
    g308: LineSegment StartX=27.9965 StartY=107.79 StartZ=0 EndX=1.57905 EndY=122.295 EndZ=0
    g309: Circle CenterX=42.5666 CenterY=-67.3492 CenterZ=0 NormalX=0 NormalY=0 NormalZ=1 AngleXU=0 Radius=1
    g310: Circle CenterX=46.0728 CenterY=-65.424 CenterZ=0 NormalX=0 NormalY=0 NormalZ=1 AngleXU=0 Radius=1
    g311: Circle CenterX=46.0728 CenterY=-69.424 CenterZ=0 NormalX=0 NormalY=0 NormalZ=1 AngleXU=0 Radius=1
    g312: BSplineCurve PolesCount=3 KnotsCount=2 Degree=2 IsPeriodic=0
    g313: GeomPoint X=42.5666 Y=-67.3492 Z=0
    g314: GeomPoint X=46.0728 Y=-69.424 Z=0
    g315: Circle CenterX=46.0728 CenterY=-87.7794 CenterZ=0 NormalX=0 NormalY=0 NormalZ=1 AngleXU=0 Radius=1
    g316: Circle CenterX=46.0728 CenterY=-91.7794 CenterZ=0 NormalX=0 NormalY=0 NormalZ=1 AngleXU=0 Radius=1
    g317: Circle CenterX=42.0728 CenterY=-91.7794 CenterZ=0 NormalX=0 NormalY=0 NormalZ=1 AngleXU=0 Radius=1
    g318: BSplineCurve PolesCount=3 KnotsCount=2 Degree=2 IsPeriodic=0
    g319: GeomPoint X=46.0728 Y=-87.7794 Z=0
    g320: GeomPoint X=42.0728 Y=-91.7794 Z=0
    g321: Circle CenterX=2.07281 CenterY=-91.7794 CenterZ=0 NormalX=0 NormalY=0 NormalZ=1 AngleXU=0 Radius=1
    g322: Circle CenterX=-1.92719 CenterY=-91.7794 CenterZ=0 NormalX=0 NormalY=0 NormalZ=1 AngleXU=0 Radius=1
    g323: Circle CenterX=1.57905 CenterY=-89.8542 CenterZ=0 NormalX=0 NormalY=0 NormalZ=1 AngleXU=0 Radius=1
    g324: BSplineCurve PolesCount=3 KnotsCount=2 Degree=2 IsPeriodic=0
    g325: GeomPoint X=2.07281 Y=-91.7794 Z=0
    g326: GeomPoint X=1.57905 Y=-89.8542 Z=0
    g327: LineSegment StartX=2.07281 StartY=-91.7794 StartZ=0 EndX=42.0728 EndY=-91.7794 EndZ=0
    g328: LineSegment StartX=46.0728 StartY=-87.7794 StartZ=0 EndX=46.0728 EndY=-69.424 EndZ=0
    g329: LineSegment StartX=42.5666 StartY=-67.3492 StartZ=0 EndX=1.57905 EndY=-89.8542 EndZ=0
    g330: Circle CenterX=322.073 CenterY=76.4095 CenterZ=0 NormalX=0 NormalY=0 NormalZ=1 AngleXU=0 Radius=4
    g331: BSplineCurve PolesCount=3 KnotsCount=2 Degree=2 IsPeriodic=0
    g332: GeomPoint X=318.073 Y=72.4095 Z=0
    g333: GeomPoint X=322.073 Y=76.4095 Z=0
    g334: Circle CenterX=375.073 CenterY=72.4095 CenterZ=0 NormalX=0 NormalY=0 NormalZ=1 AngleXU=0 Radius=1
    g335: Circle CenterX=375.073 CenterY=76.4095 CenterZ=0 NormalX=0 NormalY=0 NormalZ=1 AngleXU=0 Radius=1
    g336: Circle CenterX=371.073 CenterY=76.4095 CenterZ=0 NormalX=0 NormalY=0 NormalZ=1 AngleXU=0 Radius=1
    g337: BSplineCurve PolesCount=3 KnotsCount=2 Degree=2 IsPeriodic=0
    g338: GeomPoint X=375.073 Y=72.4095 Z=0
    g339: GeomPoint X=371.073 Y=76.4095 Z=0
    g340: LineSegment StartX=322.073 StartY=76.4095 StartZ=0 EndX=371.073 EndY=76.4095 EndZ=0
    g341: LineSegment StartX=318.073 StartY=72.4095 StartZ=0 EndX=318.073 EndY=-47.4805 EndZ=0
    g342: LineSegment StartX=375.073 StartY=72.4095 StartZ=0 EndX=375.073 EndY=-78.7896 EndZ=0
    g343: ArcOfCircle CenterX=-26.9272 CenterY=22.1087 CenterZ=0 NormalX=0 NormalY=0 NormalZ=1 AngleXU=0 Radius=4 StartAngle=5e-16 EndAngle=3.14159
    g344: LineSegment StartX=-22.9272 StartY=22.1087 StartZ=0 EndX=-18.9272 EndY=-83.7794 EndZ=0
    g345: LineSegment StartX=-34.9272 StartY=-83.7794 StartZ=0 EndX=-30.9272 EndY=22.1087 EndZ=0
    g346: ArcOfCircle CenterX=391.073 CenterY=22.1087 CenterZ=0 NormalX=0 NormalY=0 NormalZ=1 AngleXU=0 Radius=4 StartAngle=0 EndAngle=3.14159
    g347: LineSegment StartX=387.073 StartY=22.1087 StartZ=0 EndX=383.073 EndY=-83.7794 EndZ=0
    g348: LineSegment StartX=395.073 StartY=22.1087 StartZ=0 EndX=399.073 EndY=-83.7794 EndZ=0
    g349: LineSegment StartX=-10.9946 StartY=77.6538 StartZ=0 EndX=-6.74301 EndY=77.6538 EndZ=0
    g350: LineSegment StartX=-12.1541 StartY=75.7916 StartZ=0 EndX=-12.1541 EndY=71.7859 EndZ=0
    g351: LineSegment StartX=44.9306 StartY=77.4064 StartZ=0 EndX=41.1006 EndY=77.4064 EndZ=0
    g352: LineSegment StartX=47.2847 StartY=75.6847 StartZ=0 EndX=47.2847 EndY=71.644 EndZ=0
    g353: LineSegment StartX=47.0795 StartY=-50.9687 StartZ=0 EndX=47.0795 EndY=-46.9775 EndZ=0
    g354: LineSegment StartX=45.9637 StartY=-52.5996 StartZ=0 EndX=42.1012 EndY=-54.7025 EndZ=0
    g355: LineSegment StartX=-8.55304 StartY=-83.2995 StartZ=0 EndX=-4.90513 EndY=-81.5399 EndZ=0
    g356: LineSegment StartX=-11.8576 StartY=-82.2695 StartZ=0 EndX=-11.8576 EndY=-77.892 EndZ=0
  constraints (579):
    c: Coincident(g0,g2)
    c: Block(g0)
    c: Block(g1)
    c: Vertical(g3)
    c: Vertical(g4)
    c: Block(g4)
    c: Block(g3)
    c: Weight(g7) = 1
    c: Equal(g7,g8)
    c: Equal(g7,g9)
    c: InternalAlignment(g7,g10)
    c: InternalAlignment(g8,g10)
    c: InternalAlignment(g9,g10)
    c: InternalAlignment(g11,g10)
    c: InternalAlignment(g12,g10)
    c: Weight(g13) = 1
    c: Equal(g13,g14)
    c: Equal(g13,g15)
    c: InternalAlignment(g13,g16)
    c: InternalAlignment(g14,g16)
    c: InternalAlignment(g15,g16)
    c: InternalAlignment(g17,g16)
    c: InternalAlignment(g18,g16)
    c: Block(g16)
    c: Block(g10)
    c: Weight(g19) = 1
    c: Equal(g19,g20)
    c: Equal(g19,g21)
    c: InternalAlignment(g19,g22)
    c: InternalAlignment(g20,g22)
    c: InternalAlignment(g21,g22)
    c: InternalAlignment(g23,g22)
    c: InternalAlignment(g24,g22)
    c: Weight(g25) = 1
    c: Equal(g25,g26)
    c: Equal(g25,g27)
    c: InternalAlignment(g25,g28)
    c: InternalAlignment(g26,g28)
    c: InternalAlignment(g27,g28)
    c: InternalAlignment(g29,g28)
    c: InternalAlignment(g30,g28)
    c: Block(g28)
    c: Block(g22)
    c: Weight(g31) = 1
    c: Equal(g31,g32)
    c: Equal(g31,g33)
    c: InternalAlignment(g31,g34)
    c: InternalAlignment(g32,g34)
    c: InternalAlignment(g33,g34)
    c: InternalAlignment(g35,g34)
    c: InternalAlignment(g36,g34)
    c: Weight(g37) = 1
    c: Equal(g37,g38)
    c: Equal(g37,g39)
    c: InternalAlignment(g37,g40)
    c: InternalAlignment(g38,g40)
    c: InternalAlignment(g39,g40)
    c: InternalAlignment(g41,g40)
    c: InternalAlignment(g42,g40)
    c: Block(g34)
    c: Block(g40)
    c: Coincident(g43,g4)
    c: Coincident(g43,g3)
    c: Horizontal(g43)
    c: Distance(g43) = 450
    c: Coincident(g44,g4)
    c: Coincident(g44,g3)
    c: Horizontal(g44)
    c: Horizontal(g45)
    c: Coincident(g2,g45)
    c: Block(g45)
    c: Coincident(g1,g45)
    c: Weight(g46) = 1
    c: Equal(g46,g47)
    c: Equal(g46,g48)
    c: InternalAlignment(g46,g49)
    c: InternalAlignment(g47,g49)
    c: InternalAlignment(g48,g49)
    c: InternalAlignment(g50,g49)
    c: InternalAlignment(g51,g49)
    c: Block(g49)
    c: Weight(g52) = 1
    c: Equal(g52,g53)
    c: Equal(g52,g54)
    c: InternalAlignment(g52,g55)
    c: InternalAlignment(g53,g55)
    c: InternalAlignment(g54,g55)
    c: InternalAlignment(g56,g55)
    c: InternalAlignment(g57,g55)
    c: Block(g55)
    c: Weight(g58) = 1
    c: Equal(g58,g59)
    c: Equal(g58,g60)
    c: InternalAlignment(g58,g61)
    c: InternalAlignment(g59,g61)
    c: InternalAlignment(g60,g61)
    c: InternalAlignment(g62,g61)
    c: InternalAlignment(g63,g61)
    c: Block(g61)
    c: Weight(g64) = 1
    c: Equal(g64,g65)
    c: Equal(g64,g66)
    c: InternalAlignment(g64,g67)
    c: InternalAlignment(g65,g67)
    c: InternalAlignment(g66,g67)
    c: InternalAlignment(g68,g67)
    c: InternalAlignment(g69,g67)
    c: Block(g67)
    c: Weight(g70) = 1
    c: Equal(g70,g71)
    c: Equal(g70,g72)
    c: InternalAlignment(g70,g73)
    c: InternalAlignment(g71,g73)
    c: InternalAlignment(g72,g73)
    c: InternalAlignment(g74,g73)
    c: InternalAlignment(g75,g73)
    c: Weight(g76) = 1
    c: Equal(g76,g77)
    c: Equal(g76,g78)
    c: InternalAlignment(g76,g79)
    c: InternalAlignment(g77,g79)
    c: InternalAlignment(g78,g79)
    c: InternalAlignment(g80,g79)
    c: InternalAlignment(g81,g79)
    c: Block(g73)
    c: Block(g79)
    c: Coincident(g82,g73)
    c: Coincident(g82,g79)
    c: Vertical(g82)
    c: Coincident(g83,g73)
    c: Coincident(g83,g55)
    c: Coincident(g84,g55)
    c: Coincident(g84,g79)
    c: Weight(g85) = 1
    c: Equal(g85,g86)
    c: Equal(g85,g87)
    c: InternalAlignment(g85,g88)
    c: InternalAlignment(g86,g88)
    c: InternalAlignment(g87,g88)
    c: InternalAlignment(g89,g88)
    c: InternalAlignment(g90,g88)
    c: Weight(g91) = 1
    c: Equal(g91,g92)
    c: Equal(g91,g93)
    c: InternalAlignment(g91,g94)
    c: InternalAlignment(g92,g94)
    c: InternalAlignment(g93,g94)
    c: InternalAlignment(g95,g94)
    c: InternalAlignment(g96,g94)
    c: Block(g88)
    c: Block(g94)
    c: Coincident(g97,g88)
    c: Coincident(g97,g94)
    c: Vertical(g97)
    c: Coincident(g98,g88)
    c: Coincident(g98,g49)
    c: Coincident(g99,g49)
    c: Coincident(g99,g94)
    c: Weight(g100) = 1
    c: Equal(g100,g101)
    c: Equal(g100,g102)
    c: InternalAlignment(g100,g103)
    c: InternalAlignment(g101,g103)
    c: InternalAlignment(g102,g103)
    c: InternalAlignment(g104,g103)
    c: InternalAlignment(g105,g103)
    c: Weight(g106) = 1
    c: Equal(g106,g107)
    c: Equal(g106,g108)
    c: InternalAlignment(g106,g109)
    c: InternalAlignment(g107,g109)
    c: InternalAlignment(g108,g109)
    c: InternalAlignment(g110,g109)
    c: InternalAlignment(g111,g109)
    c: Block(g103)
    c: Block(g109)
    c: Coincident(g112,g103)
    c: Coincident(g112,g109)
    c: Vertical(g112)
    c: Coincident(g113,g109)
    c: Coincident(g113,g67)
    c: Coincident(g114,g67)
    c: Coincident(g114,g103)
    c: Weight(g115) = 1
    c: Equal(g115,g116)
    c: Equal(g115,g117)
    c: InternalAlignment(g115,g118)
    c: InternalAlignment(g116,g118)
    c: InternalAlignment(g117,g118)
    c: InternalAlignment(g119,g118)
    c: InternalAlignment(g120,g118)
    c: Weight(g121) = 1
    c: Equal(g121,g122)
    c: Equal(g121,g123)
    c: InternalAlignment(g121,g124)
    c: InternalAlignment(g122,g124)
    c: InternalAlignment(g123,g124)
    c: InternalAlignment(g125,g124)
    c: InternalAlignment(g126,g124)
    c: Block(g118)
    c: Block(g124)
    c: Coincident(g127,g118)
    c: Coincident(g127,g124)
    c: Vertical(g127)
    c: Coincident(g128,g124)
    c: Coincident(g128,g61)
    c: Coincident(g129,g61)
    c: Coincident(g129,g118)
    c: Weight(g130) = 1
    c: Equal(g130,g131)
    c: Equal(g130,g132)
    c: InternalAlignment(g130,g133)
    c: InternalAlignment(g131,g133)
    c: InternalAlignment(g132,g133)
    c: InternalAlignment(g134,g133)
    c: InternalAlignment(g135,g133)
    c: Weight(g136) = 1
    c: Equal(g136,g137)
    c: Equal(g136,g138)
    c: InternalAlignment(g136,g139)
    c: InternalAlignment(g137,g139)
    c: InternalAlignment(g138,g139)
    c: InternalAlignment(g140,g139)
    c: InternalAlignment(g141,g139)
    c: Weight(g142) = 1
    c: Equal(g142,g143)
    c: Equal(g142,g144)
    c: InternalAlignment(g142,g145)
    c: InternalAlignment(g143,g145)
    c: InternalAlignment(g144,g145)
    c: InternalAlignment(g146,g145)
    c: InternalAlignment(g147,g145)
    c: Weight(g148) = 1
    c: Equal(g148,g149)
    c: Equal(g148,g150)
    c: InternalAlignment(g148,g151)
    c: InternalAlignment(g149,g151)
    c: InternalAlignment(g150,g151)
    c: InternalAlignment(g152,g151)
    c: InternalAlignment(g153,g151)
    c: Block(g151)
    c: Block(g145)
    c: Block(g139)
    c: Block(g133)
    c: Coincident(g154,g28)
    c: Coincident(g154,g151)
    c: Coincident(g155,g151)
    c: Coincident(g155,g145)
    c: Horizontal(g155)
    c: Coincident(g156,g145)
    c: Coincident(g156,g28)
    c: Vertical(g156)
    c: Coincident(g157,g22)
    c: Coincident(g157,g139)
    c: Vertical(g157)
    c: Coincident(g158,g139)
    c: Coincident(g158,g133)
    c: Horizontal(g158)
    c: Coincident(g159,g133)
    c: Coincident(g159,g22)
    c: Weight(g160) = 1
    c: Equal(g160,g161)
    c: Equal(g160,g162)
    c: InternalAlignment(g160,g163)
    c: InternalAlignment(g161,g163)
    c: InternalAlignment(g162,g163)
    c: InternalAlignment(g164,g163)
    c: InternalAlignment(g165,g163)
    c: Weight(g166) = 1
    c: Equal(g166,g167)
    c: Equal(g166,g168)
    c: InternalAlignment(g166,g169)
    c: InternalAlignment(g167,g169)
    c: InternalAlignment(g168,g169)
    c: InternalAlignment(g170,g169)
    c: InternalAlignment(g171,g169)
    c: Weight(g172) = 1
    c: Equal(g172,g173)
    c: Equal(g172,g174)
    c: InternalAlignment(g172,g175)
    c: InternalAlignment(g173,g175)
    c: InternalAlignment(g174,g175)
    c: InternalAlignment(g176,g175)
    c: InternalAlignment(g177,g175)
    c: Weight(g178) = 1
    c: Equal(g178,g179)
    c: Equal(g178,g180)
    c: InternalAlignment(g178,g181)
    c: InternalAlignment(g179,g181)
    c: InternalAlignment(g180,g181)
    c: InternalAlignment(g182,g181)
    c: InternalAlignment(g183,g181)
    c: Block(g181)
    c: Block(g175)
    c: Block(g169)
    c: Block(g163)
    c: Coincident(g184,g181)
    c: Coincident(g184,g175)
    c: Horizontal(g184)
    c: Coincident(g185,g175)
    c: Coincident(g185,g10)
    c: Vertical(g185)
    c: Coincident(g186,g16)
    c: Coincident(g186,g169)
    c: Vertical(g186)
    c: Coincident(g187,g169)
    c: Coincident(g187,g163)
    c: Horizontal(g187)
    c: Coincident(g188,g163)
    c: Coincident(g188,g16)
    c: Coincident(g189,g10)
    c: Weight(g190) = 1
    c: Equal(g190,g191)
    c: Equal(g190,g192)
    c: InternalAlignment(g190,g193)
    c: InternalAlignment(g191,g193)
    c: InternalAlignment(g192,g193)
    c: InternalAlignment(g194,g193)
    c: InternalAlignment(g195,g193)
    c: Weight(g196) = 1
    c: Equal(g196,g197)
    c: Equal(g196,g198)
    c: InternalAlignment(g196,g199)
    c: InternalAlignment(g197,g199)
    c: InternalAlignment(g198,g199)
    c: InternalAlignment(g200,g199)
    c: InternalAlignment(g201,g199)
    c: Block(g199)
    c: Block(g193)
    c: Coincident(g202,g199)
    c: Coincident(g202,g34)
    c: Coincident(g203,g34)
    c: Coincident(g203,g193)
    c: Coincident(g204,g193)
    c: Coincident(g204,g199)
    c: Vertical(g204)
    c: Weight(g205) = 1
    c: Equal(g205,g206)
    c: Equal(g205,g207)
    c: InternalAlignment(g205,g208)
    c: InternalAlignment(g206,g208)
    c: InternalAlignment(g207,g208)
    c: InternalAlignment(g209,g208)
    c: InternalAlignment(g210,g208)
    c: Weight(g211) = 1
    c: Equal(g211,g212)
    c: Equal(g211,g213)
    c: InternalAlignment(g211,g214)
    c: InternalAlignment(g212,g214)
    c: InternalAlignment(g213,g214)
    c: InternalAlignment(g215,g214)
    c: InternalAlignment(g216,g214)
    c: Block(g214)
    c: Block(g208)
    c: Coincident(g217,g208)
    c: Coincident(g217,g40)
    c: Coincident(g218,g40)
    c: Coincident(g218,g214)
    c: Coincident(g219,g214)
    c: Coincident(g219,g208)
    c: Vertical(g219)
    c: Horizontal(g220)
    c: Block(g220)
    c: Vertical(g221)
    c: Block(g221)
    c: Block(g222)
    c: Weight(g223) = 1
    c: Equal(g223,g224)
    c: Equal(g223,g225)
    c: InternalAlignment(g223,g226)
    c: InternalAlignment(g224,g226)
    c: InternalAlignment(g225,g226)
    c: InternalAlignment(g227,g226)
    c: InternalAlignment(g228,g226)
    c: Weight(g229) = 1
    c: Equal(g229,g230)
    c: Equal(g229,g231)
    c: InternalAlignment(g229,g232)
    c: InternalAlignment(g230,g232)
    c: InternalAlignment(g231,g232)
    c: InternalAlignment(g233,g232)
    c: InternalAlignment(g234,g232)
    c: Weight(g235) = 1
    c: Equal(g235,g236)
    c: Equal(g235,g237)
    c: InternalAlignment(g235,g238)
    c: InternalAlignment(g236,g238)
    c: InternalAlignment(g237,g238)
    c: InternalAlignment(g239,g238)
    c: InternalAlignment(g240,g238)
    c: Weight(g241) = 1
    c: Equal(g241,g242)
    c: Equal(g241,g243)
    c: InternalAlignment(g241,g244)
    c: InternalAlignment(g242,g244)
    c: InternalAlignment(g243,g244)
    c: InternalAlignment(g245,g244)
    c: InternalAlignment(g246,g244)
    c: Block(g226)
    c: Block(g232)
    c: Block(g238)
    c: Block(g244)
    c: Coincident(g247,g232)
    c: Coincident(g247,g226)
    c: Horizontal(g247)
    c: Block(g189)
    c: Weight(g248) = 1
    c: Equal(g248,g249)
    c: Equal(g248,g250)
    c: InternalAlignment(g248,g251)
    c: InternalAlignment(g249,g251)
    c: InternalAlignment(g250,g251)
    c: InternalAlignment(g252,g251)
    c: InternalAlignment(g253,g251)
    c: Weight(g254) = 1
    c: Equal(g254,g255)
    c: Equal(g254,g256)
    c: InternalAlignment(g254,g257)
    c: InternalAlignment(g255,g257)
    c: InternalAlignment(g256,g257)
    c: InternalAlignment(g258,g257)
    c: InternalAlignment(g259,g257)
    c: Block(g251)
    c: Block(g257)
    c: Coincident(g260,g251)
    c: Coincident(g260,g257)
    c: Weight(g261) = 1
    c: Equal(g261,g262)
    c: Equal(g261,g263)
    c: InternalAlignment(g261,g264)
    c: InternalAlignment(g262,g264)
    c: InternalAlignment(g263,g264)
    c: InternalAlignment(g265,g264)
    c: InternalAlignment(g266,g264)
    c: Weight(g267) = 1
    c: Equal(g267,g268)
    c: Equal(g267,g269)
    c: InternalAlignment(g267,g270)
    c: InternalAlignment(g268,g270)
    c: InternalAlignment(g269,g270)
    c: InternalAlignment(g271,g270)
    c: InternalAlignment(g272,g270)
    c: Weight(g273) = 1
    c: Equal(g273,g274)
    c: Equal(g273,g275)
    c: InternalAlignment(g273,g276)
    c: InternalAlignment(g274,g276)
    c: InternalAlignment(g275,g276)
    c: InternalAlignment(g277,g276)
    c: InternalAlignment(g278,g276)
    c: Block(g276)
    c: Block(g270)
    c: Block(g264)
    c: Coincident(g279,g270)
    c: Coincident(g279,g264)
    c: Coincident(g280,g264)
    c: Coincident(g280,g276)
    c: Vertical(g280)
    c: Coincident(g281,g276)
    c: Coincident(g281,g270)
    c: Horizontal(g281)
    c: Weight(g282) = 1
    c: Equal(g282,g283)
    c: InternalAlignment(g282,g284)
    c: InternalAlignment(g283,g284)
    c: InternalAlignment(g285,g284)
    c: InternalAlignment(g286,g284)
    c: Weight(g287) = 1
    c: InternalAlignment(g288,g290)
    c: InternalAlignment(g289,g290)
    c: InternalAlignment(g291,g290)
    c: InternalAlignment(g292,g290)
    c: Weight(g293) = 1
    c: Equal(g293,g294)
    c: Equal(g293,g295)
    c: InternalAlignment(g293,g296)
    c: InternalAlignment(g294,g296)
    c: InternalAlignment(g295,g296)
    c: InternalAlignment(g297,g296)
    c: InternalAlignment(g298,g296)
    c: Equal(g299,g300)
    c: Equal(g299,g301)
    c: InternalAlignment(g299,g302)
    c: InternalAlignment(g300,g302)
    c: InternalAlignment(g301,g302)
    c: InternalAlignment(g303,g302)
    c: InternalAlignment(g304,g302)
    c: Block(g290)
    c: Block(g296)
    c: Block(g302)
    c: Block(g284)
    c: Coincident(g305,g284)
    c: Coincident(g305,g290)
    c: Horizontal(g305)
    c: Coincident(g306,g290)
    c: Coincident(g306,g296)
    c: Vertical(g306)
    c: Coincident(g307,g296)
    c: Coincident(g307,g302)
    c: Horizontal(g307)
    c: Coincident(g308,g302)
    c: Coincident(g308,g284)
    c: Weight(g309) = 1
    c: Equal(g309,g310)
    c: Equal(g309,g311)
    c: InternalAlignment(g309,g312)
    c: InternalAlignment(g310,g312)
    c: InternalAlignment(g311,g312)
    c: InternalAlignment(g313,g312)
    c: InternalAlignment(g314,g312)
    c: Weight(g315) = 1
    c: Equal(g315,g316)
    c: Equal(g315,g317)
    c: InternalAlignment(g315,g318)
    c: InternalAlignment(g316,g318)
    c: InternalAlignment(g317,g318)
    c: InternalAlignment(g319,g318)
    c: InternalAlignment(g320,g318)
    c: Weight(g321) = 1
    c: Equal(g321,g322)
    c: Equal(g321,g323)
    c: InternalAlignment(g321,g324)
    c: InternalAlignment(g322,g324)
    c: InternalAlignment(g323,g324)
    c: InternalAlignment(g325,g324)
    c: InternalAlignment(g326,g324)
    c: Block(g324)
    c: Block(g318)
    c: Block(g312)
    c: Coincident(g327,g324)
    c: Coincident(g327,g318)
    c: Horizontal(g327)
    c: Coincident(g328,g318)
    c: Coincident(g328,g312)
    c: Vertical(g328)
    c: Coincident(g329,g312)
    c: Coincident(g329,g324)
    c: InternalAlignment(g330,g331)
    c: InternalAlignment(g332,g331)
    c: InternalAlignment(g333,g331)
    c: Block(g331)
    c: Equal(g334,g335)
    c: Equal(g334,g336)
    c: InternalAlignment(g334,g337)
    c: InternalAlignment(g335,g337)
    c: InternalAlignment(g336,g337)
    c: InternalAlignment(g338,g337)
    c: InternalAlignment(g339,g337)
    c: Block(g337)
    c: Coincident(g340,g331)
    c: Horizontal(g340)
    c: Block(g340)
    c: Coincident(g341,g331)
    c: Coincident(g341,g257)
    c: Vertical(g341)
    c: Coincident(g342,g337)
    c: Coincident(g342,g251)
    c: Vertical(g342)
    c: Block(g343)
    c: Block(g5)
    c: Distance(g341) = 119.89
    c: Coincident(g344,g343)
    c: Coincident(g344,g5)
    c: Coincident(g345,g5)
    c: Coincident(g345,g343)
    c: Block(g6)
    c: Block(g346)
    c: Coincident(g347,g346)
    c: Coincident(g347,g6)
    c: Coincident(g348,g346)
    c: Coincident(g348,g6)
    c: Block(g348)
    c: Block(g347)
    c: Horizontal(g349)
    c: Vertical(g350)
    c: Horizontal(g351)
    c: Vertical(g352)
    c: Vertical(g353)
    c: Vertical(g356)
